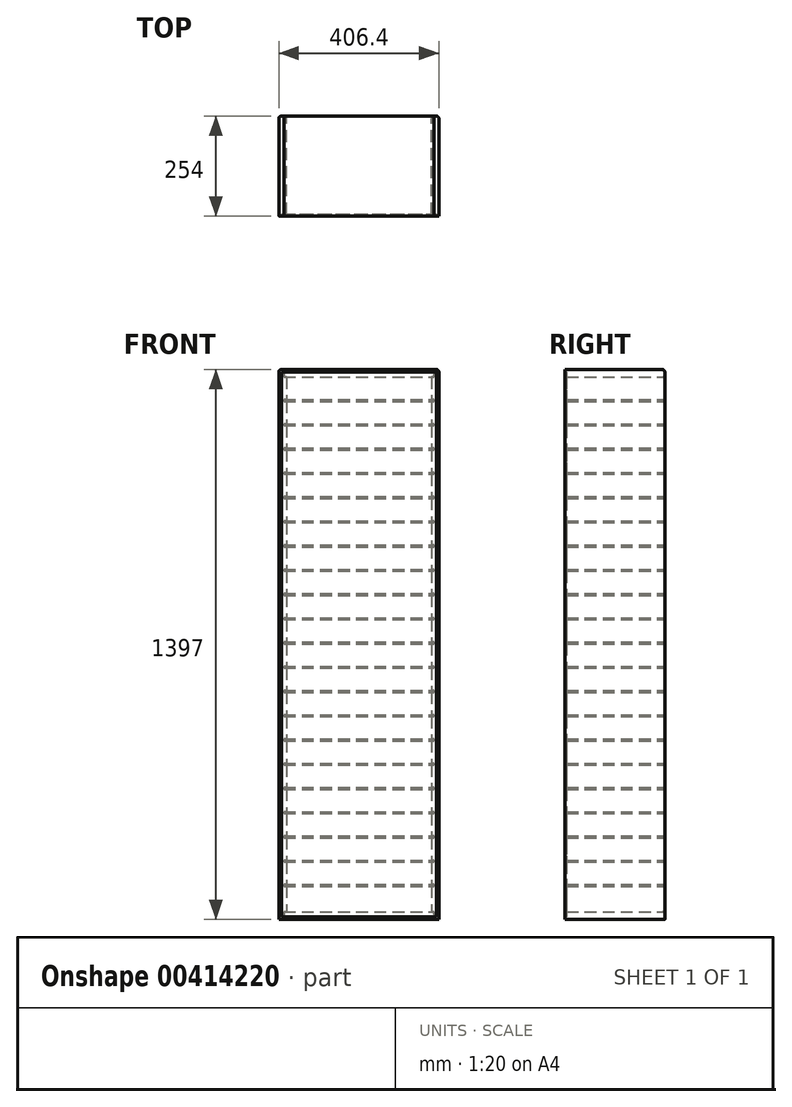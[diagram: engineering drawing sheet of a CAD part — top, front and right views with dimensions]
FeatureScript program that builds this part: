
annotation { "Feature Type Name" : "Feature", "Feature Type Description" : "" }
export const myFeature = defineFeature(function(context is Context, id is Id, definition is map)
    precondition{}
    {
        {
            var Q0;
            Q0=qCreatedBy(makeId("Front.planeOp"),FACE);
            var sketch = newSketch(context, id + "F0", { "sketchPlane" : qUnion([Q0])});
            skLineSegment(sketch, "E0.left", {"start": v(831.85, 679.45) * mm, "end": v(831.85, -679.45) * mm});
            skLineSegment(sketch, "E0.right", {"start": v(1200.15, 679.45) * mm, "end": v(1200.15, -679.45) * mm});
            skLineSegment(sketch, "E1.bottom", {"start": v(812.8, 698.5) * mm, "end": v(1219.2, 698.5) * mm});
            skLineSegment(sketch, "E1.top", {"start": v(812.8, -698.5) * mm, "end": v(1219.2, -698.5) * mm});
            skLineSegment(sketch, "E2.0", {"start": v(825.5, 679.45) * mm, "end": v(1206.5, 679.45) * mm});
            skLineSegment(sketch, "E3.bottom", {"start": v(825.5, 622.3) * mm, "end": v(1206.5, 622.3) * mm});
            skLineSegment(sketch, "E3.top", {"start": v(825.5, 617.86) * mm, "end": v(1206.5, 617.86) * mm});
            skLineSegment(sketch, "E4", {"start": v(825.5, 698.5) * mm, "end": v(825.5, 679.45) * mm});
            skLineSegment(sketch, "E5", {"start": v(1206.5, 698.5) * mm, "end": v(1206.5, 679.45) * mm});
            skLineSegment(sketch, "E6.trimOffspring", {"start": v(1219.2, 698.5) * mm, "end": v(1219.2, -698.5) * mm});
            skLineSegment(sketch, "E7.trimOffspring", {"start": v(812.8, 698.5) * mm, "end": v(812.8, -698.5) * mm});
            skLineSegment(sketch, "E8.0.1.0", {"start": v(825.5, 560.7) * mm, "end": v(825.5, 556.26) * mm});
            skLineSegment(sketch, "E8.0.1.1", {"start": v(825.5, 560.7) * mm, "end": v(1206.5, 560.7) * mm});
            skLineSegment(sketch, "E8.0.1.2", {"start": v(825.5, 556.26) * mm, "end": v(1206.5, 556.26) * mm});
            skLineSegment(sketch, "E8.0.1.3", {"start": v(1206.5, 560.7) * mm, "end": v(1206.5, 556.26) * mm});
            skLineSegment(sketch, "E8.0.2.0", {"start": v(825.5, 499.1) * mm, "end": v(825.5, 494.66) * mm});
            skLineSegment(sketch, "E8.0.2.1", {"start": v(825.5, 499.1) * mm, "end": v(1206.5, 499.1) * mm});
            skLineSegment(sketch, "E8.0.2.2", {"start": v(825.5, 494.66) * mm, "end": v(1206.5, 494.66) * mm});
            skLineSegment(sketch, "E8.0.2.3", {"start": v(1206.5, 499.1) * mm, "end": v(1206.5, 494.66) * mm});
            skLineSegment(sketch, "E8.0.3.0", {"start": v(825.5, 437.51) * mm, "end": v(825.5, 433.07) * mm});
            skLineSegment(sketch, "E8.0.3.1", {"start": v(825.5, 437.51) * mm, "end": v(1206.5, 437.51) * mm});
            skLineSegment(sketch, "E8.0.3.2", {"start": v(825.5, 433.07) * mm, "end": v(1206.5, 433.07) * mm});
            skLineSegment(sketch, "E8.0.3.3", {"start": v(1206.5, 437.51) * mm, "end": v(1206.5, 433.07) * mm});
            skLineSegment(sketch, "E8.0.4.0", {"start": v(825.5, 375.92) * mm, "end": v(825.5, 371.48) * mm});
            skLineSegment(sketch, "E8.0.4.1", {"start": v(825.5, 375.92) * mm, "end": v(1206.5, 375.92) * mm});
            skLineSegment(sketch, "E8.0.4.2", {"start": v(825.5, 371.48) * mm, "end": v(1206.5, 371.48) * mm});
            skLineSegment(sketch, "E8.0.4.3", {"start": v(1206.5, 375.92) * mm, "end": v(1206.5, 371.48) * mm});
            skLineSegment(sketch, "E8.0.5.0", {"start": v(825.5, 314.33) * mm, "end": v(825.5, 309.88) * mm});
            skLineSegment(sketch, "E8.0.5.1", {"start": v(825.5, 314.33) * mm, "end": v(1206.5, 314.33) * mm});
            skLineSegment(sketch, "E8.0.5.2", {"start": v(825.5, 309.88) * mm, "end": v(1206.5, 309.88) * mm});
            skLineSegment(sketch, "E8.0.5.3", {"start": v(1206.5, 314.33) * mm, "end": v(1206.5, 309.88) * mm});
            skLineSegment(sketch, "E8.0.6.0", {"start": v(825.5, 252.73) * mm, "end": v(825.5, 248.29) * mm});
            skLineSegment(sketch, "E8.0.6.1", {"start": v(825.5, 252.73) * mm, "end": v(1206.5, 252.73) * mm});
            skLineSegment(sketch, "E8.0.6.2", {"start": v(825.5, 248.29) * mm, "end": v(1206.5, 248.29) * mm});
            skLineSegment(sketch, "E8.0.6.3", {"start": v(1206.5, 252.73) * mm, "end": v(1206.5, 248.29) * mm});
            skLineSegment(sketch, "E8.0.7.0", {"start": v(825.5, 191.14) * mm, "end": v(825.5, 186.7) * mm});
            skLineSegment(sketch, "E8.0.7.1", {"start": v(825.5, 191.14) * mm, "end": v(1206.5, 191.14) * mm});
            skLineSegment(sketch, "E8.0.7.2", {"start": v(825.5, 186.7) * mm, "end": v(1206.5, 186.7) * mm});
            skLineSegment(sketch, "E8.0.7.3", {"start": v(1206.5, 191.14) * mm, "end": v(1206.5, 186.7) * mm});
            skLineSegment(sketch, "E8.0.8.0", {"start": v(825.5, 129.54) * mm, "end": v(825.5, 125.1) * mm});
            skLineSegment(sketch, "E8.0.8.1", {"start": v(825.5, 129.54) * mm, "end": v(1206.5, 129.54) * mm});
            skLineSegment(sketch, "E8.0.8.2", {"start": v(825.5, 125.1) * mm, "end": v(1206.5, 125.1) * mm});
            skLineSegment(sketch, "E8.0.8.3", {"start": v(1206.5, 129.54) * mm, "end": v(1206.5, 125.1) * mm});
            skLineSegment(sketch, "E8.0.9.0", {"start": v(825.5, 67.95) * mm, "end": v(825.5, 63.5) * mm});
            skLineSegment(sketch, "E8.0.9.1", {"start": v(825.5, 67.95) * mm, "end": v(1206.5, 67.95) * mm});
            skLineSegment(sketch, "E8.0.9.2", {"start": v(825.5, 63.5) * mm, "end": v(1206.5, 63.5) * mm});
            skLineSegment(sketch, "E8.0.9.3", {"start": v(1206.5, 67.95) * mm, "end": v(1206.5, 63.5) * mm});
            skLineSegment(sketch, "E8.0.10.0", {"start": v(825.5, 6.35) * mm, "end": v(825.5, 1.9) * mm});
            skLineSegment(sketch, "E8.0.10.1", {"start": v(825.5, 6.35) * mm, "end": v(1206.5, 6.35) * mm});
            skLineSegment(sketch, "E8.0.10.2", {"start": v(825.5, 1.9) * mm, "end": v(1206.5, 1.9) * mm});
            skLineSegment(sketch, "E8.0.10.3", {"start": v(1206.5, 6.35) * mm, "end": v(1206.5, 1.9) * mm});
            skLineSegment(sketch, "E8.0.11.0", {"start": v(825.5, -55.24) * mm, "end": v(825.5, -59.69) * mm});
            skLineSegment(sketch, "E8.0.11.1", {"start": v(825.5, -55.24) * mm, "end": v(1206.5, -55.24) * mm});
            skLineSegment(sketch, "E8.0.11.2", {"start": v(825.5, -59.69) * mm, "end": v(1206.5, -59.69) * mm});
            skLineSegment(sketch, "E8.0.11.3", {"start": v(1206.5, -55.24) * mm, "end": v(1206.5, -59.69) * mm});
            skLineSegment(sketch, "E8.0.12.0", {"start": v(825.5, -116.84) * mm, "end": v(825.5, -121.28) * mm});
            skLineSegment(sketch, "E8.0.12.1", {"start": v(825.5, -116.84) * mm, "end": v(1206.5, -116.84) * mm});
            skLineSegment(sketch, "E8.0.12.2", {"start": v(825.5, -121.28) * mm, "end": v(1206.5, -121.28) * mm});
            skLineSegment(sketch, "E8.0.12.3", {"start": v(1206.5, -116.84) * mm, "end": v(1206.5, -121.28) * mm});
            skLineSegment(sketch, "E8.0.13.0", {"start": v(825.5, -178.43) * mm, "end": v(825.5, -182.88) * mm});
            skLineSegment(sketch, "E8.0.13.1", {"start": v(825.5, -178.43) * mm, "end": v(1206.5, -178.43) * mm});
            skLineSegment(sketch, "E8.0.13.2", {"start": v(825.5, -182.88) * mm, "end": v(1206.5, -182.88) * mm});
            skLineSegment(sketch, "E8.0.13.3", {"start": v(1206.5, -178.43) * mm, "end": v(1206.5, -182.88) * mm});
            skLineSegment(sketch, "E8.0.14.0", {"start": v(825.5, -240.03) * mm, "end": v(825.5, -244.47) * mm});
            skLineSegment(sketch, "E8.0.14.1", {"start": v(825.5, -240.03) * mm, "end": v(1206.5, -240.03) * mm});
            skLineSegment(sketch, "E8.0.14.2", {"start": v(825.5, -244.47) * mm, "end": v(1206.5, -244.47) * mm});
            skLineSegment(sketch, "E8.0.14.3", {"start": v(1206.5, -240.03) * mm, "end": v(1206.5, -244.47) * mm});
            skLineSegment(sketch, "E8.0.15.0", {"start": v(825.5, -301.62) * mm, "end": v(825.5, -306.07) * mm});
            skLineSegment(sketch, "E8.0.15.1", {"start": v(825.5, -301.62) * mm, "end": v(1206.5, -301.62) * mm});
            skLineSegment(sketch, "E8.0.15.2", {"start": v(825.5, -306.07) * mm, "end": v(1206.5, -306.07) * mm});
            skLineSegment(sketch, "E8.0.15.3", {"start": v(1206.5, -301.62) * mm, "end": v(1206.5, -306.07) * mm});
            skLineSegment(sketch, "E8.0.16.0", {"start": v(825.5, -363.22) * mm, "end": v(825.5, -367.66) * mm});
            skLineSegment(sketch, "E8.0.16.1", {"start": v(825.5, -363.22) * mm, "end": v(1206.5, -363.22) * mm});
            skLineSegment(sketch, "E8.0.16.2", {"start": v(825.5, -367.66) * mm, "end": v(1206.5, -367.66) * mm});
            skLineSegment(sketch, "E8.0.16.3", {"start": v(1206.5, -363.22) * mm, "end": v(1206.5, -367.66) * mm});
            skLineSegment(sketch, "E8.0.17.0", {"start": v(825.5, -424.81) * mm, "end": v(825.5, -429.26) * mm});
            skLineSegment(sketch, "E8.0.17.1", {"start": v(825.5, -424.81) * mm, "end": v(1206.5, -424.81) * mm});
            skLineSegment(sketch, "E8.0.17.2", {"start": v(825.5, -429.26) * mm, "end": v(1206.5, -429.26) * mm});
            skLineSegment(sketch, "E8.0.17.3", {"start": v(1206.5, -424.81) * mm, "end": v(1206.5, -429.26) * mm});
            skLineSegment(sketch, "E8.0.18.0", {"start": v(825.5, -486.4) * mm, "end": v(825.5, -490.85) * mm});
            skLineSegment(sketch, "E8.0.18.1", {"start": v(825.5, -486.4) * mm, "end": v(1206.5, -486.4) * mm});
            skLineSegment(sketch, "E8.0.18.2", {"start": v(825.5, -490.85) * mm, "end": v(1206.5, -490.85) * mm});
            skLineSegment(sketch, "E8.0.18.3", {"start": v(1206.5, -486.4) * mm, "end": v(1206.5, -490.85) * mm});
            skLineSegment(sketch, "E8.0.19.0", {"start": v(825.5, -548) * mm, "end": v(825.5, -552.45) * mm});
            skLineSegment(sketch, "E8.0.19.1", {"start": v(825.5, -548) * mm, "end": v(1206.5, -548) * mm});
            skLineSegment(sketch, "E8.0.19.2", {"start": v(825.5, -552.45) * mm, "end": v(1206.5, -552.45) * mm});
            skLineSegment(sketch, "E8.0.19.3", {"start": v(1206.5, -548) * mm, "end": v(1206.5, -552.45) * mm});
            skLineSegment(sketch, "E8.0.20.0", {"start": v(825.5, -609.6) * mm, "end": v(825.5, -614.04) * mm});
            skLineSegment(sketch, "E8.0.20.1", {"start": v(825.5, -609.6) * mm, "end": v(1206.5, -609.6) * mm});
            skLineSegment(sketch, "E8.0.20.2", {"start": v(825.5, -614.04) * mm, "end": v(1206.5, -614.04) * mm});
            skLineSegment(sketch, "E8.0.20.3", {"start": v(1206.5, -679.45) * mm, "end": v(1206.5, -698.5) * mm});
            skLineSegment(sketch, "E8.direction1", {"start": v(825.5, 617.86) * mm, "end": v(850.9, 617.86) * mm, "construction": true});
            skLineSegment(sketch, "E9.trimOffspring", {"start": v(825.5, -679.45) * mm, "end": v(1206.5, -679.45) * mm});
            skLineSegment(sketch, "E10.trimOffspring", {"start": v(825.5, -679.45) * mm, "end": v(825.5, -698.5) * mm});
            skLineSegment(sketch, "E11", {"start": v(1206.5, -609.6) * mm, "end": v(1206.5, -614.04) * mm});
            skLineSegment(sketch, "E12.trimOffspring", {"start": v(825.5, 622.3) * mm, "end": v(825.5, 617.86) * mm});
            skLineSegment(sketch, "E13.trimOffspring", {"start": v(1206.5, 622.3) * mm, "end": v(1206.5, 617.86) * mm});
            skLineSegment(sketch, "E14", {"start": v(1219.2, 12.7) * mm, "end": v(2036.37, 12.7) * mm});
            skSolve(sketch);
        }
        {
            var Q0;
            {var subQ39=sQuery(id+"F0.wireOp",EDGE,"E4");Q0=makeQuery(id+"F0.imprint","IMPRINT",FACE,{"disambiguationData":[TD([[makeQuery(id+"F0.imprint","IMPRINT",EDGE,{"derivedFrom":subQ39}),-1.0]])]});}
            var Q1;
            {var subQ35=sQuery(id+"F0.wireOp",EDGE,"E5");Q1=makeQuery(id+"F0.imprint","IMPRINT",FACE,{"disambiguationData":[TD([[makeQuery(id+"F0.imprint","IMPRINT",EDGE,{"derivedFrom":subQ35}),1.0]])]});}
            extrude(context, id + "F1", {"entities" : qUnion([Q0, Q1]), "depth" : 254 * mm});
        }
        {
            var Q0;
            {var subQ4=sQuery(id+"F0.wireOp",EDGE,"E8.0.20.3");Q0=makeQuery(id+"F0.imprint","IMPRINT",FACE,{"disambiguationData":[TD([[makeQuery(id+"F0.imprint","IMPRINT",EDGE,{"derivedFrom":subQ4}),-1.0]])]});}
            var Q1;
            {var subQ4=sQuery(id+"F0.wireOp",EDGE,"E4");Q1=makeQuery(id+"F0.imprint","IMPRINT",FACE,{"disambiguationData":[TD([[makeQuery(id+"F0.imprint","IMPRINT",EDGE,{"derivedFrom":subQ4}),1.0]])]});}
            extrude(context, id + "F2", {"entities" : qUnion([Q0, Q1]), "depth" : 254 * mm});
        }
        {
            var Q0;
            {var subQ0=sQuery(id+"F0.wireOp",EDGE,"E3.bottom");var subQ1=sQuery(id+"F0.wireOp",EDGE,"E0.left");var subQ2=makeQuery(id+"F0.imprint","INTERSECT",VERTEX,{"derivedFrom":[subQ1,subQ0]});Q0=makeQuery(id+"F0.imprint","IMPRINT",FACE,{"disambiguationData":[TD([[makeQuery(id+"F0.imprint","IMPRINT",EDGE,{"disambiguationData":[TD([[subQ2,-1.0]])],"derivedFrom":subQ1}),1.0]])]});}
            var Q1;
            {var subQ0=sQuery(id+"F0.wireOp",EDGE,"E8.0.1.1");var subQ1=sQuery(id+"F0.wireOp",EDGE,"E0.left");var subQ2=makeQuery(id+"F0.imprint","INTERSECT",VERTEX,{"derivedFrom":[subQ1,subQ0]});Q1=makeQuery(id+"F0.imprint","IMPRINT",FACE,{"disambiguationData":[TD([[makeQuery(id+"F0.imprint","IMPRINT",EDGE,{"disambiguationData":[TD([[subQ2,-1.0]])],"derivedFrom":subQ1}),1.0]])]});}
            var Q2;
            {var subQ0=sQuery(id+"F0.wireOp",EDGE,"E8.0.2.1");var subQ1=sQuery(id+"F0.wireOp",EDGE,"E0.left");var subQ2=makeQuery(id+"F0.imprint","INTERSECT",VERTEX,{"derivedFrom":[subQ1,subQ0]});Q2=makeQuery(id+"F0.imprint","IMPRINT",FACE,{"disambiguationData":[TD([[makeQuery(id+"F0.imprint","IMPRINT",EDGE,{"disambiguationData":[TD([[subQ2,-1.0]])],"derivedFrom":subQ1}),1.0]])]});}
            var Q3;
            {var subQ0=sQuery(id+"F0.wireOp",EDGE,"E8.0.3.1");var subQ1=sQuery(id+"F0.wireOp",EDGE,"E0.left");var subQ2=makeQuery(id+"F0.imprint","INTERSECT",VERTEX,{"derivedFrom":[subQ1,subQ0]});Q3=makeQuery(id+"F0.imprint","IMPRINT",FACE,{"disambiguationData":[TD([[makeQuery(id+"F0.imprint","IMPRINT",EDGE,{"disambiguationData":[TD([[subQ2,-1.0]])],"derivedFrom":subQ1}),1.0]])]});}
            var Q4;
            {var subQ0=sQuery(id+"F0.wireOp",EDGE,"E8.0.4.1");var subQ1=sQuery(id+"F0.wireOp",EDGE,"E0.left");var subQ2=makeQuery(id+"F0.imprint","INTERSECT",VERTEX,{"derivedFrom":[subQ1,subQ0]});Q4=makeQuery(id+"F0.imprint","IMPRINT",FACE,{"disambiguationData":[TD([[makeQuery(id+"F0.imprint","IMPRINT",EDGE,{"disambiguationData":[TD([[subQ2,-1.0]])],"derivedFrom":subQ1}),1.0]])]});}
            var Q5;
            {var subQ0=sQuery(id+"F0.wireOp",EDGE,"E8.0.5.1");var subQ1=sQuery(id+"F0.wireOp",EDGE,"E0.left");var subQ2=makeQuery(id+"F0.imprint","INTERSECT",VERTEX,{"derivedFrom":[subQ1,subQ0]});Q5=makeQuery(id+"F0.imprint","IMPRINT",FACE,{"disambiguationData":[TD([[makeQuery(id+"F0.imprint","IMPRINT",EDGE,{"disambiguationData":[TD([[subQ2,-1.0]])],"derivedFrom":subQ1}),1.0]])]});}
            var Q6;
            {var subQ5=sQuery(id+"F0.wireOp",EDGE,"E13.trimOffspring");Q6=makeQuery(id+"F0.imprint","IMPRINT",FACE,{"disambiguationData":[TD([[makeQuery(id+"F0.imprint","IMPRINT",EDGE,{"derivedFrom":subQ5}),-1.0]])]});}
            var Q7;
            {var subQ5=sQuery(id+"F0.wireOp",EDGE,"E12.trimOffspring");Q7=makeQuery(id+"F0.imprint","IMPRINT",FACE,{"disambiguationData":[TD([[makeQuery(id+"F0.imprint","IMPRINT",EDGE,{"derivedFrom":subQ5}),1.0]])]});}
            var Q8;
            {var subQ5=sQuery(id+"F0.wireOp",EDGE,"E8.0.1.0");Q8=makeQuery(id+"F0.imprint","IMPRINT",FACE,{"disambiguationData":[TD([[makeQuery(id+"F0.imprint","IMPRINT",EDGE,{"derivedFrom":subQ5}),1.0]])]});}
            var Q9;
            {var subQ5=sQuery(id+"F0.wireOp",EDGE,"E8.0.1.3");Q9=makeQuery(id+"F0.imprint","IMPRINT",FACE,{"disambiguationData":[TD([[makeQuery(id+"F0.imprint","IMPRINT",EDGE,{"derivedFrom":subQ5}),-1.0]])]});}
            var Q10;
            {var subQ5=sQuery(id+"F0.wireOp",EDGE,"E8.0.2.3");Q10=makeQuery(id+"F0.imprint","IMPRINT",FACE,{"disambiguationData":[TD([[makeQuery(id+"F0.imprint","IMPRINT",EDGE,{"derivedFrom":subQ5}),-1.0]])]});}
            var Q11;
            {var subQ5=sQuery(id+"F0.wireOp",EDGE,"E8.0.2.0");Q11=makeQuery(id+"F0.imprint","IMPRINT",FACE,{"disambiguationData":[TD([[makeQuery(id+"F0.imprint","IMPRINT",EDGE,{"derivedFrom":subQ5}),1.0]])]});}
            var Q12;
            {var subQ5=sQuery(id+"F0.wireOp",EDGE,"E8.0.3.0");Q12=makeQuery(id+"F0.imprint","IMPRINT",FACE,{"disambiguationData":[TD([[makeQuery(id+"F0.imprint","IMPRINT",EDGE,{"derivedFrom":subQ5}),1.0]])]});}
            var Q13;
            {var subQ5=sQuery(id+"F0.wireOp",EDGE,"E8.0.3.3");Q13=makeQuery(id+"F0.imprint","IMPRINT",FACE,{"disambiguationData":[TD([[makeQuery(id+"F0.imprint","IMPRINT",EDGE,{"derivedFrom":subQ5}),-1.0]])]});}
            var Q14;
            {var subQ5=sQuery(id+"F0.wireOp",EDGE,"E8.0.4.3");Q14=makeQuery(id+"F0.imprint","IMPRINT",FACE,{"disambiguationData":[TD([[makeQuery(id+"F0.imprint","IMPRINT",EDGE,{"derivedFrom":subQ5}),-1.0]])]});}
            var Q15;
            {var subQ5=sQuery(id+"F0.wireOp",EDGE,"E8.0.4.0");Q15=makeQuery(id+"F0.imprint","IMPRINT",FACE,{"disambiguationData":[TD([[makeQuery(id+"F0.imprint","IMPRINT",EDGE,{"derivedFrom":subQ5}),1.0]])]});}
            var Q16;
            {var subQ5=sQuery(id+"F0.wireOp",EDGE,"E8.0.5.3");Q16=makeQuery(id+"F0.imprint","IMPRINT",FACE,{"disambiguationData":[TD([[makeQuery(id+"F0.imprint","IMPRINT",EDGE,{"derivedFrom":subQ5}),-1.0]])]});}
            var Q17;
            {var subQ5=sQuery(id+"F0.wireOp",EDGE,"E8.0.5.0");Q17=makeQuery(id+"F0.imprint","IMPRINT",FACE,{"disambiguationData":[TD([[makeQuery(id+"F0.imprint","IMPRINT",EDGE,{"derivedFrom":subQ5}),1.0]])]});}
            var Q18;
            {var subQ5=sQuery(id+"F0.wireOp",EDGE,"E8.0.6.0");Q18=makeQuery(id+"F0.imprint","IMPRINT",FACE,{"disambiguationData":[TD([[makeQuery(id+"F0.imprint","IMPRINT",EDGE,{"derivedFrom":subQ5}),1.0]])]});}
            var Q19;
            {var subQ0=sQuery(id+"F0.wireOp",EDGE,"E8.0.6.1");var subQ1=sQuery(id+"F0.wireOp",EDGE,"E0.left");var subQ2=makeQuery(id+"F0.imprint","INTERSECT",VERTEX,{"derivedFrom":[subQ1,subQ0]});Q19=makeQuery(id+"F0.imprint","IMPRINT",FACE,{"disambiguationData":[TD([[makeQuery(id+"F0.imprint","IMPRINT",EDGE,{"disambiguationData":[TD([[subQ2,-1.0]])],"derivedFrom":subQ1}),1.0]])]});}
            var Q20;
            {var subQ5=sQuery(id+"F0.wireOp",EDGE,"E8.0.6.3");Q20=makeQuery(id+"F0.imprint","IMPRINT",FACE,{"disambiguationData":[TD([[makeQuery(id+"F0.imprint","IMPRINT",EDGE,{"derivedFrom":subQ5}),-1.0]])]});}
            var Q21;
            {var subQ5=sQuery(id+"F0.wireOp",EDGE,"E8.0.7.3");Q21=makeQuery(id+"F0.imprint","IMPRINT",FACE,{"disambiguationData":[TD([[makeQuery(id+"F0.imprint","IMPRINT",EDGE,{"derivedFrom":subQ5}),-1.0]])]});}
            var Q22;
            {var subQ0=sQuery(id+"F0.wireOp",EDGE,"E8.0.7.1");var subQ1=sQuery(id+"F0.wireOp",EDGE,"E0.left");var subQ2=makeQuery(id+"F0.imprint","INTERSECT",VERTEX,{"derivedFrom":[subQ1,subQ0]});Q22=makeQuery(id+"F0.imprint","IMPRINT",FACE,{"disambiguationData":[TD([[makeQuery(id+"F0.imprint","IMPRINT",EDGE,{"disambiguationData":[TD([[subQ2,-1.0]])],"derivedFrom":subQ1}),1.0]])]});}
            var Q23;
            {var subQ5=sQuery(id+"F0.wireOp",EDGE,"E8.0.7.0");Q23=makeQuery(id+"F0.imprint","IMPRINT",FACE,{"disambiguationData":[TD([[makeQuery(id+"F0.imprint","IMPRINT",EDGE,{"derivedFrom":subQ5}),1.0]])]});}
            var Q24;
            {var subQ5=sQuery(id+"F0.wireOp",EDGE,"E8.0.8.3");Q24=makeQuery(id+"F0.imprint","IMPRINT",FACE,{"disambiguationData":[TD([[makeQuery(id+"F0.imprint","IMPRINT",EDGE,{"derivedFrom":subQ5}),-1.0]])]});}
            var Q25;
            {var subQ0=sQuery(id+"F0.wireOp",EDGE,"E8.0.8.1");var subQ1=sQuery(id+"F0.wireOp",EDGE,"E0.left");var subQ2=makeQuery(id+"F0.imprint","INTERSECT",VERTEX,{"derivedFrom":[subQ1,subQ0]});Q25=makeQuery(id+"F0.imprint","IMPRINT",FACE,{"disambiguationData":[TD([[makeQuery(id+"F0.imprint","IMPRINT",EDGE,{"disambiguationData":[TD([[subQ2,-1.0]])],"derivedFrom":subQ1}),1.0]])]});}
            var Q26;
            {var subQ5=sQuery(id+"F0.wireOp",EDGE,"E8.0.8.0");Q26=makeQuery(id+"F0.imprint","IMPRINT",FACE,{"disambiguationData":[TD([[makeQuery(id+"F0.imprint","IMPRINT",EDGE,{"derivedFrom":subQ5}),1.0]])]});}
            var Q27;
            {var subQ5=sQuery(id+"F0.wireOp",EDGE,"E8.0.9.0");Q27=makeQuery(id+"F0.imprint","IMPRINT",FACE,{"disambiguationData":[TD([[makeQuery(id+"F0.imprint","IMPRINT",EDGE,{"derivedFrom":subQ5}),1.0]])]});}
            var Q28;
            {var subQ0=sQuery(id+"F0.wireOp",EDGE,"E8.0.9.1");var subQ1=sQuery(id+"F0.wireOp",EDGE,"E0.left");var subQ2=makeQuery(id+"F0.imprint","INTERSECT",VERTEX,{"derivedFrom":[subQ1,subQ0]});Q28=makeQuery(id+"F0.imprint","IMPRINT",FACE,{"disambiguationData":[TD([[makeQuery(id+"F0.imprint","IMPRINT",EDGE,{"disambiguationData":[TD([[subQ2,-1.0]])],"derivedFrom":subQ1}),1.0]])]});}
            var Q29;
            {var subQ5=sQuery(id+"F0.wireOp",EDGE,"E8.0.9.3");Q29=makeQuery(id+"F0.imprint","IMPRINT",FACE,{"disambiguationData":[TD([[makeQuery(id+"F0.imprint","IMPRINT",EDGE,{"derivedFrom":subQ5}),-1.0]])]});}
            var Q30;
            {var subQ5=sQuery(id+"F0.wireOp",EDGE,"E8.0.10.3");Q30=makeQuery(id+"F0.imprint","IMPRINT",FACE,{"disambiguationData":[TD([[makeQuery(id+"F0.imprint","IMPRINT",EDGE,{"derivedFrom":subQ5}),-1.0]])]});}
            var Q31;
            {var subQ0=sQuery(id+"F0.wireOp",EDGE,"E8.0.10.1");var subQ1=sQuery(id+"F0.wireOp",EDGE,"E0.left");var subQ2=makeQuery(id+"F0.imprint","INTERSECT",VERTEX,{"derivedFrom":[subQ1,subQ0]});Q31=makeQuery(id+"F0.imprint","IMPRINT",FACE,{"disambiguationData":[TD([[makeQuery(id+"F0.imprint","IMPRINT",EDGE,{"disambiguationData":[TD([[subQ2,-1.0]])],"derivedFrom":subQ1}),1.0]])]});}
            var Q32;
            {var subQ5=sQuery(id+"F0.wireOp",EDGE,"E8.0.10.0");Q32=makeQuery(id+"F0.imprint","IMPRINT",FACE,{"disambiguationData":[TD([[makeQuery(id+"F0.imprint","IMPRINT",EDGE,{"derivedFrom":subQ5}),1.0]])]});}
            var Q33;
            {var subQ5=sQuery(id+"F0.wireOp",EDGE,"E8.0.11.3");Q33=makeQuery(id+"F0.imprint","IMPRINT",FACE,{"disambiguationData":[TD([[makeQuery(id+"F0.imprint","IMPRINT",EDGE,{"derivedFrom":subQ5}),-1.0]])]});}
            var Q34;
            {var subQ0=sQuery(id+"F0.wireOp",EDGE,"E8.0.11.1");var subQ1=sQuery(id+"F0.wireOp",EDGE,"E0.left");var subQ2=makeQuery(id+"F0.imprint","INTERSECT",VERTEX,{"derivedFrom":[subQ1,subQ0]});Q34=makeQuery(id+"F0.imprint","IMPRINT",FACE,{"disambiguationData":[TD([[makeQuery(id+"F0.imprint","IMPRINT",EDGE,{"disambiguationData":[TD([[subQ2,-1.0]])],"derivedFrom":subQ1}),1.0]])]});}
            var Q35;
            {var subQ5=sQuery(id+"F0.wireOp",EDGE,"E8.0.11.0");Q35=makeQuery(id+"F0.imprint","IMPRINT",FACE,{"disambiguationData":[TD([[makeQuery(id+"F0.imprint","IMPRINT",EDGE,{"derivedFrom":subQ5}),1.0]])]});}
            var Q36;
            {var subQ5=sQuery(id+"F0.wireOp",EDGE,"E8.0.12.0");Q36=makeQuery(id+"F0.imprint","IMPRINT",FACE,{"disambiguationData":[TD([[makeQuery(id+"F0.imprint","IMPRINT",EDGE,{"derivedFrom":subQ5}),1.0]])]});}
            var Q37;
            {var subQ0=sQuery(id+"F0.wireOp",EDGE,"E8.0.12.1");var subQ1=sQuery(id+"F0.wireOp",EDGE,"E0.left");var subQ2=makeQuery(id+"F0.imprint","INTERSECT",VERTEX,{"derivedFrom":[subQ1,subQ0]});Q37=makeQuery(id+"F0.imprint","IMPRINT",FACE,{"disambiguationData":[TD([[makeQuery(id+"F0.imprint","IMPRINT",EDGE,{"disambiguationData":[TD([[subQ2,-1.0]])],"derivedFrom":subQ1}),1.0]])]});}
            var Q38;
            {var subQ5=sQuery(id+"F0.wireOp",EDGE,"E8.0.12.3");Q38=makeQuery(id+"F0.imprint","IMPRINT",FACE,{"disambiguationData":[TD([[makeQuery(id+"F0.imprint","IMPRINT",EDGE,{"derivedFrom":subQ5}),-1.0]])]});}
            var Q39;
            {var subQ5=sQuery(id+"F0.wireOp",EDGE,"E8.0.13.3");Q39=makeQuery(id+"F0.imprint","IMPRINT",FACE,{"disambiguationData":[TD([[makeQuery(id+"F0.imprint","IMPRINT",EDGE,{"derivedFrom":subQ5}),-1.0]])]});}
            var Q40;
            {var subQ0=sQuery(id+"F0.wireOp",EDGE,"E8.0.13.1");var subQ1=sQuery(id+"F0.wireOp",EDGE,"E0.left");var subQ2=makeQuery(id+"F0.imprint","INTERSECT",VERTEX,{"derivedFrom":[subQ1,subQ0]});Q40=makeQuery(id+"F0.imprint","IMPRINT",FACE,{"disambiguationData":[TD([[makeQuery(id+"F0.imprint","IMPRINT",EDGE,{"disambiguationData":[TD([[subQ2,-1.0]])],"derivedFrom":subQ1}),1.0]])]});}
            var Q41;
            {var subQ5=sQuery(id+"F0.wireOp",EDGE,"E8.0.13.0");Q41=makeQuery(id+"F0.imprint","IMPRINT",FACE,{"disambiguationData":[TD([[makeQuery(id+"F0.imprint","IMPRINT",EDGE,{"derivedFrom":subQ5}),1.0]])]});}
            var Q42;
            {var subQ5=sQuery(id+"F0.wireOp",EDGE,"E8.0.14.0");Q42=makeQuery(id+"F0.imprint","IMPRINT",FACE,{"disambiguationData":[TD([[makeQuery(id+"F0.imprint","IMPRINT",EDGE,{"derivedFrom":subQ5}),1.0]])]});}
            var Q43;
            {var subQ0=sQuery(id+"F0.wireOp",EDGE,"E8.0.14.1");var subQ1=sQuery(id+"F0.wireOp",EDGE,"E0.left");var subQ2=makeQuery(id+"F0.imprint","INTERSECT",VERTEX,{"derivedFrom":[subQ1,subQ0]});Q43=makeQuery(id+"F0.imprint","IMPRINT",FACE,{"disambiguationData":[TD([[makeQuery(id+"F0.imprint","IMPRINT",EDGE,{"disambiguationData":[TD([[subQ2,-1.0]])],"derivedFrom":subQ1}),1.0]])]});}
            var Q44;
            {var subQ5=sQuery(id+"F0.wireOp",EDGE,"E8.0.14.3");Q44=makeQuery(id+"F0.imprint","IMPRINT",FACE,{"disambiguationData":[TD([[makeQuery(id+"F0.imprint","IMPRINT",EDGE,{"derivedFrom":subQ5}),-1.0]])]});}
            var Q45;
            {var subQ5=sQuery(id+"F0.wireOp",EDGE,"E8.0.15.3");Q45=makeQuery(id+"F0.imprint","IMPRINT",FACE,{"disambiguationData":[TD([[makeQuery(id+"F0.imprint","IMPRINT",EDGE,{"derivedFrom":subQ5}),-1.0]])]});}
            var Q46;
            {var subQ0=sQuery(id+"F0.wireOp",EDGE,"E8.0.15.1");var subQ1=sQuery(id+"F0.wireOp",EDGE,"E0.left");var subQ2=makeQuery(id+"F0.imprint","INTERSECT",VERTEX,{"derivedFrom":[subQ1,subQ0]});Q46=makeQuery(id+"F0.imprint","IMPRINT",FACE,{"disambiguationData":[TD([[makeQuery(id+"F0.imprint","IMPRINT",EDGE,{"disambiguationData":[TD([[subQ2,-1.0]])],"derivedFrom":subQ1}),1.0]])]});}
            var Q47;
            {var subQ5=sQuery(id+"F0.wireOp",EDGE,"E8.0.15.0");Q47=makeQuery(id+"F0.imprint","IMPRINT",FACE,{"disambiguationData":[TD([[makeQuery(id+"F0.imprint","IMPRINT",EDGE,{"derivedFrom":subQ5}),1.0]])]});}
            var Q48;
            {var subQ0=sQuery(id+"F0.wireOp",EDGE,"E8.0.16.1");var subQ1=sQuery(id+"F0.wireOp",EDGE,"E0.left");var subQ2=makeQuery(id+"F0.imprint","INTERSECT",VERTEX,{"derivedFrom":[subQ1,subQ0]});Q48=makeQuery(id+"F0.imprint","IMPRINT",FACE,{"disambiguationData":[TD([[makeQuery(id+"F0.imprint","IMPRINT",EDGE,{"disambiguationData":[TD([[subQ2,-1.0]])],"derivedFrom":subQ1}),1.0]])]});}
            var Q49;
            {var subQ5=sQuery(id+"F0.wireOp",EDGE,"E8.0.16.3");Q49=makeQuery(id+"F0.imprint","IMPRINT",FACE,{"disambiguationData":[TD([[makeQuery(id+"F0.imprint","IMPRINT",EDGE,{"derivedFrom":subQ5}),-1.0]])]});}
            var Q50;
            {var subQ5=sQuery(id+"F0.wireOp",EDGE,"E8.0.17.3");Q50=makeQuery(id+"F0.imprint","IMPRINT",FACE,{"disambiguationData":[TD([[makeQuery(id+"F0.imprint","IMPRINT",EDGE,{"derivedFrom":subQ5}),-1.0]])]});}
            var Q51;
            {var subQ0=sQuery(id+"F0.wireOp",EDGE,"E8.0.17.1");var subQ1=sQuery(id+"F0.wireOp",EDGE,"E0.left");var subQ2=makeQuery(id+"F0.imprint","INTERSECT",VERTEX,{"derivedFrom":[subQ1,subQ0]});Q51=makeQuery(id+"F0.imprint","IMPRINT",FACE,{"disambiguationData":[TD([[makeQuery(id+"F0.imprint","IMPRINT",EDGE,{"disambiguationData":[TD([[subQ2,-1.0]])],"derivedFrom":subQ1}),1.0]])]});}
            var Q52;
            {var subQ5=sQuery(id+"F0.wireOp",EDGE,"E8.0.18.3");Q52=makeQuery(id+"F0.imprint","IMPRINT",FACE,{"disambiguationData":[TD([[makeQuery(id+"F0.imprint","IMPRINT",EDGE,{"derivedFrom":subQ5}),-1.0]])]});}
            var Q53;
            {var subQ0=sQuery(id+"F0.wireOp",EDGE,"E8.0.18.1");var subQ1=sQuery(id+"F0.wireOp",EDGE,"E0.left");var subQ2=makeQuery(id+"F0.imprint","INTERSECT",VERTEX,{"derivedFrom":[subQ1,subQ0]});Q53=makeQuery(id+"F0.imprint","IMPRINT",FACE,{"disambiguationData":[TD([[makeQuery(id+"F0.imprint","IMPRINT",EDGE,{"disambiguationData":[TD([[subQ2,-1.0]])],"derivedFrom":subQ1}),1.0]])]});}
            var Q54;
            {var subQ5=sQuery(id+"F0.wireOp",EDGE,"E8.0.16.0");Q54=makeQuery(id+"F0.imprint","IMPRINT",FACE,{"disambiguationData":[TD([[makeQuery(id+"F0.imprint","IMPRINT",EDGE,{"derivedFrom":subQ5}),1.0]])]});}
            var Q55;
            {var subQ5=sQuery(id+"F0.wireOp",EDGE,"E8.0.17.0");Q55=makeQuery(id+"F0.imprint","IMPRINT",FACE,{"disambiguationData":[TD([[makeQuery(id+"F0.imprint","IMPRINT",EDGE,{"derivedFrom":subQ5}),1.0]])]});}
            var Q56;
            {var subQ5=sQuery(id+"F0.wireOp",EDGE,"E8.0.18.0");Q56=makeQuery(id+"F0.imprint","IMPRINT",FACE,{"disambiguationData":[TD([[makeQuery(id+"F0.imprint","IMPRINT",EDGE,{"derivedFrom":subQ5}),1.0]])]});}
            var Q57;
            {var subQ5=sQuery(id+"F0.wireOp",EDGE,"E8.0.19.3");Q57=makeQuery(id+"F0.imprint","IMPRINT",FACE,{"disambiguationData":[TD([[makeQuery(id+"F0.imprint","IMPRINT",EDGE,{"derivedFrom":subQ5}),-1.0]])]});}
            var Q58;
            {var subQ0=sQuery(id+"F0.wireOp",EDGE,"E8.0.19.1");var subQ1=sQuery(id+"F0.wireOp",EDGE,"E0.left");var subQ2=makeQuery(id+"F0.imprint","INTERSECT",VERTEX,{"derivedFrom":[subQ1,subQ0]});Q58=makeQuery(id+"F0.imprint","IMPRINT",FACE,{"disambiguationData":[TD([[makeQuery(id+"F0.imprint","IMPRINT",EDGE,{"disambiguationData":[TD([[subQ2,-1.0]])],"derivedFrom":subQ1}),1.0]])]});}
            var Q59;
            {var subQ5=sQuery(id+"F0.wireOp",EDGE,"E8.0.19.0");Q59=makeQuery(id+"F0.imprint","IMPRINT",FACE,{"disambiguationData":[TD([[makeQuery(id+"F0.imprint","IMPRINT",EDGE,{"derivedFrom":subQ5}),1.0]])]});}
            var Q60;
            {var subQ0=sQuery(id+"F0.wireOp",EDGE,"E8.0.20.1");var subQ1=sQuery(id+"F0.wireOp",EDGE,"E0.left");var subQ2=makeQuery(id+"F0.imprint","INTERSECT",VERTEX,{"derivedFrom":[subQ1,subQ0]});Q60=makeQuery(id+"F0.imprint","IMPRINT",FACE,{"disambiguationData":[TD([[makeQuery(id+"F0.imprint","IMPRINT",EDGE,{"disambiguationData":[TD([[subQ2,-1.0]])],"derivedFrom":subQ1}),1.0]])]});}
            var Q61;
            {var subQ5=sQuery(id+"F0.wireOp",EDGE,"E8.0.20.0");Q61=makeQuery(id+"F0.imprint","IMPRINT",FACE,{"disambiguationData":[TD([[makeQuery(id+"F0.imprint","IMPRINT",EDGE,{"derivedFrom":subQ5}),1.0]])]});}
            var Q62;
            {var subQ5=sQuery(id+"F0.wireOp",EDGE,"E11");Q62=makeQuery(id+"F0.imprint","IMPRINT",FACE,{"disambiguationData":[TD([[makeQuery(id+"F0.imprint","IMPRINT",EDGE,{"derivedFrom":subQ5}),-1.0]])]});}
            extrude(context, id + "F3", {"entities" : qUnion([Q0, Q1, Q2, Q3, Q4, Q5, Q6, Q7, Q8, Q9, Q10, Q11, Q12, Q13, Q14, Q15, Q16, Q17, Q18, Q19, Q20, Q21, Q22, Q23, Q24, Q25, Q26, Q27, Q28, Q29, Q30, Q31, Q32, Q33, Q34, Q35, Q36, Q37, Q38, Q39, Q40, Q41, Q42, Q43, Q44, Q45, Q46, Q47, Q48, Q49, Q50, Q51, Q52, Q53, Q54, Q55, Q56, Q57, Q58, Q59, Q60, Q61, Q62]), "depth" : 254 * mm});
        }
        {
            var Q0;
            Q0=makeQuery(id+"F2.opExtrude","CAP_FACE",FACE,{"disambiguationData":[OSD([sQuery(id+"F0.wireOp",EDGE,"E1.bottom"),sQuery(id+"F0.wireOp",EDGE,"E2.0"),sQuery(id+"F0.wireOp",EDGE,"E4"),sQuery(id+"F0.wireOp",EDGE,"E5")])],"isStart":false});
            var sketch = newSketch(context, id + "F4", { "sketchPlane" : qUnion([Q0])});
            skLineSegment(sketch, "E15.0", {"start": v(812.8, 698.5) * mm, "end": v(1219.2, 698.5) * mm});
            skLineSegment(sketch, "E15.1", {"start": v(1219.2, 698.5) * mm, "end": v(1219.2, -698.5) * mm});
            skLineSegment(sketch, "E15.2", {"start": v(812.8, 698.5) * mm, "end": v(812.8, -698.5) * mm});
            skLineSegment(sketch, "E15.3", {"start": v(812.8, -698.5) * mm, "end": v(1219.2, -698.5) * mm});
            skLineSegment(sketch, "E16.0", {"start": v(819.15, 692.15) * mm, "end": v(819.15, -692.15) * mm});
            skLineSegment(sketch, "E16.1", {"start": v(819.15, 692.15) * mm, "end": v(1212.85, 692.15) * mm});
            skLineSegment(sketch, "E16.2", {"start": v(1212.85, 692.15) * mm, "end": v(1212.85, -692.15) * mm});
            skLineSegment(sketch, "E16.3", {"start": v(819.15, -692.15) * mm, "end": v(1212.85, -692.15) * mm});
            skSolve(sketch);
        }
        {
            var Q0;
            {var subQ4=sQuery(id+"F4.wireOp",EDGE,"E16.0");Q0=makeQuery(id+"F4.imprint","IMPRINT",FACE,{"disambiguationData":[TD([[makeQuery(id+"F4.imprint","IMPRINT",EDGE,{"derivedFrom":subQ4}),1.0]])]});}
            var Q1;
            {var subQ5=makeQuery(id+"F2.opExtrude","CAP_EDGE",EDGE,{"disambiguationData":[OSD([sQuery(id+"F0.wireOp",EDGE,"E2.0")])],"isStart":false});Q1=makeQuery(id+"F4.imprint","IMPRINT",FACE,{"disambiguationData":[TD([[makeQuery(id+"F4.imprint","IMPRINT",EDGE,{"derivedFrom":subQ5}),1.0]])]});}
            extrude(context, id + "F5", {"entities" : qUnion([Q0, Q1]), "oppositeDirection" : true, "depth" : 4.44 * mm});
        }
        {
            var Q0;
            Q0=makeQuery(id+"F5.opExtrude","SWEPT_BODY",BODY,{"disambiguationData":[OSD([sQuery(id+"F4.wireOp",EDGE,"E16.0"),sQuery(id+"F4.wireOp",EDGE,"E16.1"),sQuery(id+"F4.wireOp",EDGE,"E16.2"),sQuery(id+"F4.wireOp",EDGE,"E16.3")])]});
            var Q1;
            Q1=makeQuery(id+"F1.opExtrude","SWEPT_BODY",BODY,{"disambiguationData":[OSD([sQuery(id+"F0.wireOp",EDGE,"E0.left"),sQuery(id+"F0.wireOp",EDGE,"E1.bottom"),sQuery(id+"F0.wireOp",EDGE,"E1.top"),sQuery(id+"F0.wireOp",EDGE,"E2.0"),sQuery(id+"F0.wireOp",EDGE,"E3.bottom"),sQuery(id+"F0.wireOp",EDGE,"E3.top"),sQuery(id+"F0.wireOp",EDGE,"E4"),sQuery(id+"F0.wireOp",EDGE,"E7.trimOffspring"),sQuery(id+"F0.wireOp",EDGE,"E8.0.1.0"),sQuery(id+"F0.wireOp",EDGE,"E8.0.1.1"),sQuery(id+"F0.wireOp",EDGE,"E8.0.1.2"),sQuery(id+"F0.wireOp",EDGE,"E8.0.2.0"),sQuery(id+"F0.wireOp",EDGE,"E8.0.2.1"),sQuery(id+"F0.wireOp",EDGE,"E8.0.2.2"),sQuery(id+"F0.wireOp",EDGE,"E8.0.3.0"),sQuery(id+"F0.wireOp",EDGE,"E8.0.3.1"),sQuery(id+"F0.wireOp",EDGE,"E8.0.3.2"),sQuery(id+"F0.wireOp",EDGE,"E8.0.4.0"),sQuery(id+"F0.wireOp",EDGE,"E8.0.4.1"),sQuery(id+"F0.wireOp",EDGE,"E8.0.4.2"),sQuery(id+"F0.wireOp",EDGE,"E8.0.5.0"),sQuery(id+"F0.wireOp",EDGE,"E8.0.5.1"),sQuery(id+"F0.wireOp",EDGE,"E8.0.5.2"),sQuery(id+"F0.wireOp",EDGE,"E8.0.6.0"),sQuery(id+"F0.wireOp",EDGE,"E8.0.6.1"),sQuery(id+"F0.wireOp",EDGE,"E8.0.6.2"),sQuery(id+"F0.wireOp",EDGE,"E8.0.7.0"),sQuery(id+"F0.wireOp",EDGE,"E8.0.7.1"),sQuery(id+"F0.wireOp",EDGE,"E8.0.7.2"),sQuery(id+"F0.wireOp",EDGE,"E8.0.8.0"),sQuery(id+"F0.wireOp",EDGE,"E8.0.8.1"),sQuery(id+"F0.wireOp",EDGE,"E8.0.8.2"),sQuery(id+"F0.wireOp",EDGE,"E8.0.9.0"),sQuery(id+"F0.wireOp",EDGE,"E8.0.9.1"),sQuery(id+"F0.wireOp",EDGE,"E8.0.9.2"),sQuery(id+"F0.wireOp",EDGE,"E8.0.10.0"),sQuery(id+"F0.wireOp",EDGE,"E8.0.10.1"),sQuery(id+"F0.wireOp",EDGE,"E8.0.10.2"),sQuery(id+"F0.wireOp",EDGE,"E8.0.11.0"),sQuery(id+"F0.wireOp",EDGE,"E8.0.11.1"),sQuery(id+"F0.wireOp",EDGE,"E8.0.11.2"),sQuery(id+"F0.wireOp",EDGE,"E8.0.12.0"),sQuery(id+"F0.wireOp",EDGE,"E8.0.12.1"),sQuery(id+"F0.wireOp",EDGE,"E8.0.12.2"),sQuery(id+"F0.wireOp",EDGE,"E8.0.13.0"),sQuery(id+"F0.wireOp",EDGE,"E8.0.13.1"),sQuery(id+"F0.wireOp",EDGE,"E8.0.13.2"),sQuery(id+"F0.wireOp",EDGE,"E8.0.14.0"),sQuery(id+"F0.wireOp",EDGE,"E8.0.14.1"),sQuery(id+"F0.wireOp",EDGE,"E8.0.14.2"),sQuery(id+"F0.wireOp",EDGE,"E8.0.15.0"),sQuery(id+"F0.wireOp",EDGE,"E8.0.15.1"),sQuery(id+"F0.wireOp",EDGE,"E8.0.15.2"),sQuery(id+"F0.wireOp",EDGE,"E8.0.16.0"),sQuery(id+"F0.wireOp",EDGE,"E8.0.16.1"),sQuery(id+"F0.wireOp",EDGE,"E8.0.16.2"),sQuery(id+"F0.wireOp",EDGE,"E8.0.17.0"),sQuery(id+"F0.wireOp",EDGE,"E8.0.17.1"),sQuery(id+"F0.wireOp",EDGE,"E8.0.17.2"),sQuery(id+"F0.wireOp",EDGE,"E8.0.18.0"),sQuery(id+"F0.wireOp",EDGE,"E8.0.18.1"),sQuery(id+"F0.wireOp",EDGE,"E8.0.18.2"),sQuery(id+"F0.wireOp",EDGE,"E8.0.19.0"),sQuery(id+"F0.wireOp",EDGE,"E8.0.19.1"),sQuery(id+"F0.wireOp",EDGE,"E8.0.19.2"),sQuery(id+"F0.wireOp",EDGE,"E8.0.20.0"),sQuery(id+"F0.wireOp",EDGE,"E8.0.20.1"),sQuery(id+"F0.wireOp",EDGE,"E8.0.20.2"),sQuery(id+"F0.wireOp",EDGE,"E9.trimOffspring"),sQuery(id+"F0.wireOp",EDGE,"E10.trimOffspring"),sQuery(id+"F0.wireOp",EDGE,"E12.trimOffspring")])]});
            var Q2;
            Q2=makeQuery(id+"F1.opExtrude","SWEPT_BODY",BODY,{"disambiguationData":[OSD([sQuery(id+"F0.wireOp",EDGE,"E0.right"),sQuery(id+"F0.wireOp",EDGE,"E1.bottom"),sQuery(id+"F0.wireOp",EDGE,"E1.top"),sQuery(id+"F0.wireOp",EDGE,"E2.0"),sQuery(id+"F0.wireOp",EDGE,"E3.bottom"),sQuery(id+"F0.wireOp",EDGE,"E3.top"),sQuery(id+"F0.wireOp",EDGE,"E5"),sQuery(id+"F0.wireOp",EDGE,"E6.trimOffspring"),sQuery(id+"F0.wireOp",EDGE,"E8.0.1.1"),sQuery(id+"F0.wireOp",EDGE,"E8.0.1.2"),sQuery(id+"F0.wireOp",EDGE,"E8.0.1.3"),sQuery(id+"F0.wireOp",EDGE,"E8.0.2.1"),sQuery(id+"F0.wireOp",EDGE,"E8.0.2.2"),sQuery(id+"F0.wireOp",EDGE,"E8.0.2.3"),sQuery(id+"F0.wireOp",EDGE,"E8.0.3.1"),sQuery(id+"F0.wireOp",EDGE,"E8.0.3.2"),sQuery(id+"F0.wireOp",EDGE,"E8.0.3.3"),sQuery(id+"F0.wireOp",EDGE,"E8.0.4.1"),sQuery(id+"F0.wireOp",EDGE,"E8.0.4.2"),sQuery(id+"F0.wireOp",EDGE,"E8.0.4.3"),sQuery(id+"F0.wireOp",EDGE,"E8.0.5.1"),sQuery(id+"F0.wireOp",EDGE,"E8.0.5.2"),sQuery(id+"F0.wireOp",EDGE,"E8.0.5.3"),sQuery(id+"F0.wireOp",EDGE,"E8.0.6.1"),sQuery(id+"F0.wireOp",EDGE,"E8.0.6.2"),sQuery(id+"F0.wireOp",EDGE,"E8.0.6.3"),sQuery(id+"F0.wireOp",EDGE,"E8.0.7.1"),sQuery(id+"F0.wireOp",EDGE,"E8.0.7.2"),sQuery(id+"F0.wireOp",EDGE,"E8.0.7.3"),sQuery(id+"F0.wireOp",EDGE,"E8.0.8.1"),sQuery(id+"F0.wireOp",EDGE,"E8.0.8.2"),sQuery(id+"F0.wireOp",EDGE,"E8.0.8.3"),sQuery(id+"F0.wireOp",EDGE,"E8.0.9.1"),sQuery(id+"F0.wireOp",EDGE,"E8.0.9.2"),sQuery(id+"F0.wireOp",EDGE,"E8.0.9.3"),sQuery(id+"F0.wireOp",EDGE,"E8.0.10.1"),sQuery(id+"F0.wireOp",EDGE,"E8.0.10.2"),sQuery(id+"F0.wireOp",EDGE,"E8.0.10.3"),sQuery(id+"F0.wireOp",EDGE,"E8.0.11.1"),sQuery(id+"F0.wireOp",EDGE,"E8.0.11.2"),sQuery(id+"F0.wireOp",EDGE,"E8.0.11.3"),sQuery(id+"F0.wireOp",EDGE,"E8.0.12.1"),sQuery(id+"F0.wireOp",EDGE,"E8.0.12.2"),sQuery(id+"F0.wireOp",EDGE,"E8.0.12.3"),sQuery(id+"F0.wireOp",EDGE,"E8.0.13.1"),sQuery(id+"F0.wireOp",EDGE,"E8.0.13.2"),sQuery(id+"F0.wireOp",EDGE,"E8.0.13.3"),sQuery(id+"F0.wireOp",EDGE,"E8.0.14.1"),sQuery(id+"F0.wireOp",EDGE,"E8.0.14.2"),sQuery(id+"F0.wireOp",EDGE,"E8.0.14.3"),sQuery(id+"F0.wireOp",EDGE,"E8.0.15.1"),sQuery(id+"F0.wireOp",EDGE,"E8.0.15.2"),sQuery(id+"F0.wireOp",EDGE,"E8.0.15.3"),sQuery(id+"F0.wireOp",EDGE,"E8.0.16.1"),sQuery(id+"F0.wireOp",EDGE,"E8.0.16.2"),sQuery(id+"F0.wireOp",EDGE,"E8.0.16.3"),sQuery(id+"F0.wireOp",EDGE,"E8.0.17.1"),sQuery(id+"F0.wireOp",EDGE,"E8.0.17.2"),sQuery(id+"F0.wireOp",EDGE,"E8.0.17.3"),sQuery(id+"F0.wireOp",EDGE,"E8.0.18.1"),sQuery(id+"F0.wireOp",EDGE,"E8.0.18.2"),sQuery(id+"F0.wireOp",EDGE,"E8.0.18.3"),sQuery(id+"F0.wireOp",EDGE,"E8.0.19.1"),sQuery(id+"F0.wireOp",EDGE,"E8.0.19.2"),sQuery(id+"F0.wireOp",EDGE,"E8.0.19.3"),sQuery(id+"F0.wireOp",EDGE,"E8.0.20.1"),sQuery(id+"F0.wireOp",EDGE,"E8.0.20.2"),sQuery(id+"F0.wireOp",EDGE,"E8.0.20.3"),sQuery(id+"F0.wireOp",EDGE,"E9.trimOffspring"),sQuery(id+"F0.wireOp",EDGE,"E11"),sQuery(id+"F0.wireOp",EDGE,"E13.trimOffspring")])]});
            var Q3;
            Q3=makeQuery(id+"F2.opExtrude","SWEPT_BODY",BODY,{"disambiguationData":[OSD([sQuery(id+"F0.wireOp",EDGE,"E1.bottom"),sQuery(id+"F0.wireOp",EDGE,"E2.0"),sQuery(id+"F0.wireOp",EDGE,"E4"),sQuery(id+"F0.wireOp",EDGE,"E5")])]});
            var Q4;
            Q4=makeQuery(id+"F2.opExtrude","SWEPT_BODY",BODY,{"disambiguationData":[OSD([sQuery(id+"F0.wireOp",EDGE,"E1.top"),sQuery(id+"F0.wireOp",EDGE,"E8.0.20.3"),sQuery(id+"F0.wireOp",EDGE,"E9.trimOffspring"),sQuery(id+"F0.wireOp",EDGE,"E10.trimOffspring")])]});
            var Q5;
            Q5=makeQuery(id+"F3.opExtrude","SWEPT_BODY",BODY,{"disambiguationData":[OSD([sQuery(id+"F0.wireOp",EDGE,"E0.right"),sQuery(id+"F0.wireOp",EDGE,"E8.0.20.0"),sQuery(id+"F0.wireOp",EDGE,"E8.0.20.1"),sQuery(id+"F0.wireOp",EDGE,"E8.0.20.2")])]});
            var Q6;
            Q6=makeQuery(id+"F3.opExtrude","SWEPT_BODY",BODY,{"disambiguationData":[OSD([sQuery(id+"F0.wireOp",EDGE,"E3.bottom"),sQuery(id+"F0.wireOp",EDGE,"E3.top"),sQuery(id+"F0.wireOp",EDGE,"E12.trimOffspring"),sQuery(id+"F0.wireOp",EDGE,"E13.trimOffspring")])]});
            var Q7;
            Q7=makeQuery(id+"F3.opExtrude","SWEPT_BODY",BODY,{"disambiguationData":[OSD([sQuery(id+"F0.wireOp",EDGE,"E8.0.1.0"),sQuery(id+"F0.wireOp",EDGE,"E8.0.1.1"),sQuery(id+"F0.wireOp",EDGE,"E8.0.1.2"),sQuery(id+"F0.wireOp",EDGE,"E8.0.1.3")])]});
            var Q8;
            Q8=makeQuery(id+"F3.opExtrude","SWEPT_BODY",BODY,{"disambiguationData":[OSD([sQuery(id+"F0.wireOp",EDGE,"E8.0.2.0"),sQuery(id+"F0.wireOp",EDGE,"E8.0.2.1"),sQuery(id+"F0.wireOp",EDGE,"E8.0.2.2"),sQuery(id+"F0.wireOp",EDGE,"E8.0.2.3")])]});
            var Q9;
            Q9=makeQuery(id+"F3.opExtrude","SWEPT_BODY",BODY,{"disambiguationData":[OSD([sQuery(id+"F0.wireOp",EDGE,"E8.0.3.0"),sQuery(id+"F0.wireOp",EDGE,"E8.0.3.1"),sQuery(id+"F0.wireOp",EDGE,"E8.0.3.2"),sQuery(id+"F0.wireOp",EDGE,"E8.0.3.3")])]});
            var Q10;
            Q10=makeQuery(id+"F3.opExtrude","SWEPT_BODY",BODY,{"disambiguationData":[OSD([sQuery(id+"F0.wireOp",EDGE,"E8.0.4.0"),sQuery(id+"F0.wireOp",EDGE,"E8.0.4.1"),sQuery(id+"F0.wireOp",EDGE,"E8.0.4.2"),sQuery(id+"F0.wireOp",EDGE,"E8.0.4.3")])]});
            var Q11;
            Q11=makeQuery(id+"F3.opExtrude","SWEPT_BODY",BODY,{"disambiguationData":[OSD([sQuery(id+"F0.wireOp",EDGE,"E8.0.5.0"),sQuery(id+"F0.wireOp",EDGE,"E8.0.5.1"),sQuery(id+"F0.wireOp",EDGE,"E8.0.5.2"),sQuery(id+"F0.wireOp",EDGE,"E8.0.5.3")])]});
            var Q12;
            Q12=makeQuery(id+"F3.opExtrude","SWEPT_BODY",BODY,{"disambiguationData":[OSD([sQuery(id+"F0.wireOp",EDGE,"E8.0.6.0"),sQuery(id+"F0.wireOp",EDGE,"E8.0.6.1"),sQuery(id+"F0.wireOp",EDGE,"E8.0.6.2"),sQuery(id+"F0.wireOp",EDGE,"E8.0.6.3")])]});
            var Q13;
            Q13=makeQuery(id+"F3.opExtrude","SWEPT_BODY",BODY,{"disambiguationData":[OSD([sQuery(id+"F0.wireOp",EDGE,"E8.0.7.0"),sQuery(id+"F0.wireOp",EDGE,"E8.0.7.1"),sQuery(id+"F0.wireOp",EDGE,"E8.0.7.2"),sQuery(id+"F0.wireOp",EDGE,"E8.0.7.3")])]});
            var Q14;
            Q14=makeQuery(id+"F3.opExtrude","SWEPT_BODY",BODY,{"disambiguationData":[OSD([sQuery(id+"F0.wireOp",EDGE,"E8.0.8.0"),sQuery(id+"F0.wireOp",EDGE,"E8.0.8.1"),sQuery(id+"F0.wireOp",EDGE,"E8.0.8.2"),sQuery(id+"F0.wireOp",EDGE,"E8.0.8.3")])]});
            var Q15;
            Q15=makeQuery(id+"F3.opExtrude","SWEPT_BODY",BODY,{"disambiguationData":[OSD([sQuery(id+"F0.wireOp",EDGE,"E8.0.9.0"),sQuery(id+"F0.wireOp",EDGE,"E8.0.9.1"),sQuery(id+"F0.wireOp",EDGE,"E8.0.9.2"),sQuery(id+"F0.wireOp",EDGE,"E8.0.9.3")])]});
            var Q16;
            Q16=makeQuery(id+"F3.opExtrude","SWEPT_BODY",BODY,{"disambiguationData":[OSD([sQuery(id+"F0.wireOp",EDGE,"E8.0.10.0"),sQuery(id+"F0.wireOp",EDGE,"E8.0.10.1"),sQuery(id+"F0.wireOp",EDGE,"E8.0.10.2"),sQuery(id+"F0.wireOp",EDGE,"E8.0.10.3")])]});
            var Q17;
            Q17=makeQuery(id+"F3.opExtrude","SWEPT_BODY",BODY,{"disambiguationData":[OSD([sQuery(id+"F0.wireOp",EDGE,"E8.0.11.0"),sQuery(id+"F0.wireOp",EDGE,"E8.0.11.1"),sQuery(id+"F0.wireOp",EDGE,"E8.0.11.2"),sQuery(id+"F0.wireOp",EDGE,"E8.0.11.3")])]});
            var Q18;
            Q18=makeQuery(id+"F3.opExtrude","SWEPT_BODY",BODY,{"disambiguationData":[OSD([sQuery(id+"F0.wireOp",EDGE,"E8.0.12.0"),sQuery(id+"F0.wireOp",EDGE,"E8.0.12.1"),sQuery(id+"F0.wireOp",EDGE,"E8.0.12.2"),sQuery(id+"F0.wireOp",EDGE,"E8.0.12.3")])]});
            var Q19;
            Q19=makeQuery(id+"F3.opExtrude","SWEPT_BODY",BODY,{"disambiguationData":[OSD([sQuery(id+"F0.wireOp",EDGE,"E8.0.13.0"),sQuery(id+"F0.wireOp",EDGE,"E8.0.13.1"),sQuery(id+"F0.wireOp",EDGE,"E8.0.13.2"),sQuery(id+"F0.wireOp",EDGE,"E8.0.13.3")])]});
            var Q20;
            Q20=makeQuery(id+"F3.opExtrude","SWEPT_BODY",BODY,{"disambiguationData":[OSD([sQuery(id+"F0.wireOp",EDGE,"E8.0.14.0"),sQuery(id+"F0.wireOp",EDGE,"E8.0.14.1"),sQuery(id+"F0.wireOp",EDGE,"E8.0.14.2"),sQuery(id+"F0.wireOp",EDGE,"E8.0.14.3")])]});
            var Q21;
            Q21=makeQuery(id+"F3.opExtrude","SWEPT_BODY",BODY,{"disambiguationData":[OSD([sQuery(id+"F0.wireOp",EDGE,"E8.0.15.0"),sQuery(id+"F0.wireOp",EDGE,"E8.0.15.1"),sQuery(id+"F0.wireOp",EDGE,"E8.0.15.2"),sQuery(id+"F0.wireOp",EDGE,"E8.0.15.3")])]});
            var Q22;
            Q22=makeQuery(id+"F3.opExtrude","SWEPT_BODY",BODY,{"disambiguationData":[OSD([sQuery(id+"F0.wireOp",EDGE,"E8.0.16.0"),sQuery(id+"F0.wireOp",EDGE,"E8.0.16.1"),sQuery(id+"F0.wireOp",EDGE,"E8.0.16.2"),sQuery(id+"F0.wireOp",EDGE,"E8.0.16.3")])]});
            var Q23;
            Q23=makeQuery(id+"F3.opExtrude","SWEPT_BODY",BODY,{"disambiguationData":[OSD([sQuery(id+"F0.wireOp",EDGE,"E8.0.17.0"),sQuery(id+"F0.wireOp",EDGE,"E8.0.17.1"),sQuery(id+"F0.wireOp",EDGE,"E8.0.17.2"),sQuery(id+"F0.wireOp",EDGE,"E8.0.17.3")])]});
            var Q24;
            Q24=makeQuery(id+"F3.opExtrude","SWEPT_BODY",BODY,{"disambiguationData":[OSD([sQuery(id+"F0.wireOp",EDGE,"E8.0.18.0"),sQuery(id+"F0.wireOp",EDGE,"E8.0.18.1"),sQuery(id+"F0.wireOp",EDGE,"E8.0.18.2"),sQuery(id+"F0.wireOp",EDGE,"E8.0.18.3")])]});
            var Q25;
            Q25=makeQuery(id+"F3.opExtrude","SWEPT_BODY",BODY,{"disambiguationData":[OSD([sQuery(id+"F0.wireOp",EDGE,"E8.0.19.0"),sQuery(id+"F0.wireOp",EDGE,"E8.0.19.1"),sQuery(id+"F0.wireOp",EDGE,"E8.0.19.2"),sQuery(id+"F0.wireOp",EDGE,"E8.0.19.3")])]});
            booleanBodies(context, id + "F6", {"operationType" : BooleanOperationType.SUBTRACTION, "tools" : qUnion([Q0]), "targets" : qUnion([Q1, Q2, Q3, Q4, Q5, Q6, Q7, Q8, Q9, Q10, Q11, Q12, Q13, Q14, Q15, Q16, Q17, Q18, Q19, Q20, Q21, Q22, Q23, Q24, Q25]), "keepTools" : true});
        }
        {
            var Q0;
            Q0=makeQuery(id+"F2.opExtrude","CAP_EDGE",EDGE,{"disambiguationData":[OSD([sQuery(id+"F0.wireOp",EDGE,"E1.bottom")])],"isStart":true});
            var Q1;
            Q1=makeQuery(id+"F1.opExtrude","SWEPT_EDGE",EDGE,{"disambiguationData":[OSD([sQuery(id+"F0.wireOp",EDGE,"E1.bottom"),sQuery(id+"F0.wireOp",EDGE,"E6.trimOffspring")])]});
            var Q2;
            Q2=makeQuery(id+"F1.opExtrude","SWEPT_EDGE",EDGE,{"disambiguationData":[OSD([sQuery(id+"F0.wireOp",EDGE,"E1.bottom"),sQuery(id+"F0.wireOp",EDGE,"E7.trimOffspring")])]});
            var Q3;
            {var subQ0=sQuery(id+"F0.wireOp",EDGE,"E1.bottom");Q3=makeQuery(id+"F1.opExtrude","CAP_EDGE",EDGE,{"disambiguationData":[OSD([subQ0]),TDD([makeQuery(id+"F0.imprint","IMPRINT",EDGE,{"disambiguationData":[TD([[makeQuery(id+"F0.imprint","INTERSECT",VERTEX,{"derivedFrom":[subQ0,sQuery(id+"F0.wireOp",EDGE,"E7.trimOffspring")]}),-1.0]])],"derivedFrom":subQ0})])],"isStart":true});}
            var Q4;
            {var subQ0=sQuery(id+"F0.wireOp",EDGE,"E1.bottom");Q4=makeQuery(id+"F1.opExtrude","CAP_EDGE",EDGE,{"disambiguationData":[OSD([subQ0]),TDD([makeQuery(id+"F0.imprint","IMPRINT",EDGE,{"disambiguationData":[TD([[makeQuery(id+"F0.imprint","INTERSECT",VERTEX,{"derivedFrom":[subQ0,sQuery(id+"F0.wireOp",EDGE,"E6.trimOffspring")]}),1.0]])],"derivedFrom":subQ0})])],"isStart":true});}
            var Q5;
            Q5=makeQuery(id+"F1.opExtrude","CAP_EDGE",EDGE,{"disambiguationData":[OSD([sQuery(id+"F0.wireOp",EDGE,"E6.trimOffspring")])],"isStart":true});
            var Q6;
            Q6=makeQuery(id+"F1.opExtrude","CAP_EDGE",EDGE,{"disambiguationData":[OSD([sQuery(id+"F0.wireOp",EDGE,"E7.trimOffspring")])],"isStart":true});
            var Q7;
            {var subQ0=sQuery(id+"F0.wireOp",EDGE,"E0.right");Q7=makeQuery(id+"F1.opExtrude","CAP_EDGE",EDGE,{"disambiguationData":[OSD([subQ0]),TDD([makeQuery(id+"F0.imprint","IMPRINT",EDGE,{"disambiguationData":[TD([[makeQuery(id+"F0.imprint","INTERSECT",VERTEX,{"derivedFrom":[subQ0,sQuery(id+"F0.wireOp",EDGE,"E2.0")]}),-1.0]])],"derivedFrom":subQ0})])],"isStart":true});}
            var Q8;
            {var subQ0=sQuery(id+"F0.wireOp",EDGE,"E0.right");Q8=makeQuery(id+"F1.opExtrude","CAP_EDGE",EDGE,{"disambiguationData":[OSD([subQ0]),TDD([makeQuery(id+"F0.imprint","IMPRINT",EDGE,{"disambiguationData":[TD([[makeQuery(id+"F0.imprint","INTERSECT",VERTEX,{"derivedFrom":[subQ0,sQuery(id+"F0.wireOp",EDGE,"E3.top")]}),-1.0]])],"derivedFrom":subQ0})])],"isStart":true});}
            var Q9;
            {var subQ0=sQuery(id+"F0.wireOp",EDGE,"E0.left");Q9=makeQuery(id+"F1.opExtrude","CAP_EDGE",EDGE,{"disambiguationData":[OSD([subQ0]),TDD([makeQuery(id+"F0.imprint","IMPRINT",EDGE,{"disambiguationData":[TD([[makeQuery(id+"F0.imprint","INTERSECT",VERTEX,{"derivedFrom":[subQ0,sQuery(id+"F0.wireOp",EDGE,"E2.0")]}),-1.0]])],"derivedFrom":subQ0})])],"isStart":true});}
            var Q10;
            {var subQ0=sQuery(id+"F0.wireOp",EDGE,"E0.left");Q10=makeQuery(id+"F1.opExtrude","CAP_EDGE",EDGE,{"disambiguationData":[OSD([subQ0]),TDD([makeQuery(id+"F0.imprint","IMPRINT",EDGE,{"disambiguationData":[TD([[makeQuery(id+"F0.imprint","INTERSECT",VERTEX,{"derivedFrom":[subQ0,sQuery(id+"F0.wireOp",EDGE,"E3.top")]}),-1.0]])],"derivedFrom":subQ0})])],"isStart":true});}
            var Q11;
            {var subQ0=sQuery(id+"F0.wireOp",EDGE,"E0.left");Q11=makeQuery(id+"F1.opExtrude","CAP_EDGE",EDGE,{"disambiguationData":[OSD([subQ0]),TDD([makeQuery(id+"F0.imprint","IMPRINT",EDGE,{"disambiguationData":[TD([[makeQuery(id+"F0.imprint","INTERSECT",VERTEX,{"derivedFrom":[subQ0,sQuery(id+"F0.wireOp",EDGE,"E8.0.1.2")]}),-1.0]])],"derivedFrom":subQ0})])],"isStart":true});}
            var Q12;
            {var subQ0=sQuery(id+"F0.wireOp",EDGE,"E0.right");Q12=makeQuery(id+"F1.opExtrude","CAP_EDGE",EDGE,{"disambiguationData":[OSD([subQ0]),TDD([makeQuery(id+"F0.imprint","IMPRINT",EDGE,{"disambiguationData":[TD([[makeQuery(id+"F0.imprint","INTERSECT",VERTEX,{"derivedFrom":[subQ0,sQuery(id+"F0.wireOp",EDGE,"E8.0.1.2")]}),-1.0]])],"derivedFrom":subQ0})])],"isStart":true});}
            var Q13;
            {var subQ0=sQuery(id+"F0.wireOp",EDGE,"E0.right");Q13=makeQuery(id+"F1.opExtrude","CAP_EDGE",EDGE,{"disambiguationData":[OSD([subQ0]),TDD([makeQuery(id+"F0.imprint","IMPRINT",EDGE,{"disambiguationData":[TD([[makeQuery(id+"F0.imprint","INTERSECT",VERTEX,{"derivedFrom":[subQ0,sQuery(id+"F0.wireOp",EDGE,"E8.0.2.2")]}),-1.0]])],"derivedFrom":subQ0})])],"isStart":true});}
            var Q14;
            {var subQ0=sQuery(id+"F0.wireOp",EDGE,"E0.right");Q14=makeQuery(id+"F1.opExtrude","CAP_EDGE",EDGE,{"disambiguationData":[OSD([subQ0]),TDD([makeQuery(id+"F0.imprint","IMPRINT",EDGE,{"disambiguationData":[TD([[makeQuery(id+"F0.imprint","INTERSECT",VERTEX,{"derivedFrom":[subQ0,sQuery(id+"F0.wireOp",EDGE,"E8.0.3.2")]}),-1.0]])],"derivedFrom":subQ0})])],"isStart":true});}
            var Q15;
            {var subQ0=sQuery(id+"F0.wireOp",EDGE,"E0.right");Q15=makeQuery(id+"F1.opExtrude","CAP_EDGE",EDGE,{"disambiguationData":[OSD([subQ0]),TDD([makeQuery(id+"F0.imprint","IMPRINT",EDGE,{"disambiguationData":[TD([[makeQuery(id+"F0.imprint","INTERSECT",VERTEX,{"derivedFrom":[subQ0,sQuery(id+"F0.wireOp",EDGE,"E8.0.4.2")]}),-1.0]])],"derivedFrom":subQ0})])],"isStart":true});}
            var Q16;
            {var subQ0=sQuery(id+"F0.wireOp",EDGE,"E0.right");Q16=makeQuery(id+"F1.opExtrude","CAP_EDGE",EDGE,{"disambiguationData":[OSD([subQ0]),TDD([makeQuery(id+"F0.imprint","IMPRINT",EDGE,{"disambiguationData":[TD([[makeQuery(id+"F0.imprint","INTERSECT",VERTEX,{"derivedFrom":[subQ0,sQuery(id+"F0.wireOp",EDGE,"E8.0.5.2")]}),-1.0]])],"derivedFrom":subQ0})])],"isStart":true});}
            var Q17;
            {var subQ0=sQuery(id+"F0.wireOp",EDGE,"E0.right");Q17=makeQuery(id+"F1.opExtrude","CAP_EDGE",EDGE,{"disambiguationData":[OSD([subQ0]),TDD([makeQuery(id+"F0.imprint","IMPRINT",EDGE,{"disambiguationData":[TD([[makeQuery(id+"F0.imprint","INTERSECT",VERTEX,{"derivedFrom":[subQ0,sQuery(id+"F0.wireOp",EDGE,"E8.0.6.2")]}),-1.0]])],"derivedFrom":subQ0})])],"isStart":true});}
            var Q18;
            {var subQ0=sQuery(id+"F0.wireOp",EDGE,"E0.right");Q18=makeQuery(id+"F1.opExtrude","CAP_EDGE",EDGE,{"disambiguationData":[OSD([subQ0]),TDD([makeQuery(id+"F0.imprint","IMPRINT",EDGE,{"disambiguationData":[TD([[makeQuery(id+"F0.imprint","INTERSECT",VERTEX,{"derivedFrom":[subQ0,sQuery(id+"F0.wireOp",EDGE,"E8.0.7.2")]}),-1.0]])],"derivedFrom":subQ0})])],"isStart":true});}
            var Q19;
            {var subQ0=sQuery(id+"F0.wireOp",EDGE,"E0.right");Q19=makeQuery(id+"F1.opExtrude","CAP_EDGE",EDGE,{"disambiguationData":[OSD([subQ0]),TDD([makeQuery(id+"F0.imprint","IMPRINT",EDGE,{"disambiguationData":[TD([[makeQuery(id+"F0.imprint","INTERSECT",VERTEX,{"derivedFrom":[subQ0,sQuery(id+"F0.wireOp",EDGE,"E8.0.8.2")]}),-1.0]])],"derivedFrom":subQ0})])],"isStart":true});}
            var Q20;
            {var subQ0=sQuery(id+"F0.wireOp",EDGE,"E0.right");Q20=makeQuery(id+"F1.opExtrude","CAP_EDGE",EDGE,{"disambiguationData":[OSD([subQ0]),TDD([makeQuery(id+"F0.imprint","IMPRINT",EDGE,{"disambiguationData":[TD([[makeQuery(id+"F0.imprint","INTERSECT",VERTEX,{"derivedFrom":[subQ0,sQuery(id+"F0.wireOp",EDGE,"E8.0.9.2")]}),-1.0]])],"derivedFrom":subQ0})])],"isStart":true});}
            var Q21;
            {var subQ0=sQuery(id+"F0.wireOp",EDGE,"E0.right");Q21=makeQuery(id+"F1.opExtrude","CAP_EDGE",EDGE,{"disambiguationData":[OSD([subQ0]),TDD([makeQuery(id+"F0.imprint","IMPRINT",EDGE,{"disambiguationData":[TD([[makeQuery(id+"F0.imprint","INTERSECT",VERTEX,{"derivedFrom":[subQ0,sQuery(id+"F0.wireOp",EDGE,"E8.0.10.2")]}),-1.0]])],"derivedFrom":subQ0})])],"isStart":true});}
            var Q22;
            {var subQ0=sQuery(id+"F0.wireOp",EDGE,"E0.right");Q22=makeQuery(id+"F1.opExtrude","CAP_EDGE",EDGE,{"disambiguationData":[OSD([subQ0]),TDD([makeQuery(id+"F0.imprint","IMPRINT",EDGE,{"disambiguationData":[TD([[makeQuery(id+"F0.imprint","INTERSECT",VERTEX,{"derivedFrom":[subQ0,sQuery(id+"F0.wireOp",EDGE,"E8.0.11.2")]}),-1.0]])],"derivedFrom":subQ0})])],"isStart":true});}
            var Q23;
            {var subQ0=sQuery(id+"F0.wireOp",EDGE,"E0.right");Q23=makeQuery(id+"F1.opExtrude","CAP_EDGE",EDGE,{"disambiguationData":[OSD([subQ0]),TDD([makeQuery(id+"F0.imprint","IMPRINT",EDGE,{"disambiguationData":[TD([[makeQuery(id+"F0.imprint","INTERSECT",VERTEX,{"derivedFrom":[subQ0,sQuery(id+"F0.wireOp",EDGE,"E8.0.12.2")]}),-1.0]])],"derivedFrom":subQ0})])],"isStart":true});}
            var Q24;
            {var subQ0=sQuery(id+"F0.wireOp",EDGE,"E0.right");Q24=makeQuery(id+"F1.opExtrude","CAP_EDGE",EDGE,{"disambiguationData":[OSD([subQ0]),TDD([makeQuery(id+"F0.imprint","IMPRINT",EDGE,{"disambiguationData":[TD([[makeQuery(id+"F0.imprint","INTERSECT",VERTEX,{"derivedFrom":[subQ0,sQuery(id+"F0.wireOp",EDGE,"E8.0.13.2")]}),-1.0]])],"derivedFrom":subQ0})])],"isStart":true});}
            var Q25;
            {var subQ0=sQuery(id+"F0.wireOp",EDGE,"E0.right");Q25=makeQuery(id+"F1.opExtrude","CAP_EDGE",EDGE,{"disambiguationData":[OSD([subQ0]),TDD([makeQuery(id+"F0.imprint","IMPRINT",EDGE,{"disambiguationData":[TD([[makeQuery(id+"F0.imprint","INTERSECT",VERTEX,{"derivedFrom":[subQ0,sQuery(id+"F0.wireOp",EDGE,"E8.0.14.2")]}),-1.0]])],"derivedFrom":subQ0})])],"isStart":true});}
            var Q26;
            {var subQ0=sQuery(id+"F0.wireOp",EDGE,"E0.right");Q26=makeQuery(id+"F1.opExtrude","CAP_EDGE",EDGE,{"disambiguationData":[OSD([subQ0]),TDD([makeQuery(id+"F0.imprint","IMPRINT",EDGE,{"disambiguationData":[TD([[makeQuery(id+"F0.imprint","INTERSECT",VERTEX,{"derivedFrom":[subQ0,sQuery(id+"F0.wireOp",EDGE,"E8.0.15.2")]}),-1.0]])],"derivedFrom":subQ0})])],"isStart":true});}
            var Q27;
            {var subQ0=sQuery(id+"F0.wireOp",EDGE,"E0.right");Q27=makeQuery(id+"F1.opExtrude","CAP_EDGE",EDGE,{"disambiguationData":[OSD([subQ0]),TDD([makeQuery(id+"F0.imprint","IMPRINT",EDGE,{"disambiguationData":[TD([[makeQuery(id+"F0.imprint","INTERSECT",VERTEX,{"derivedFrom":[subQ0,sQuery(id+"F0.wireOp",EDGE,"E8.0.17.2")]}),-1.0]])],"derivedFrom":subQ0})])],"isStart":true});}
            var Q28;
            {var subQ0=sQuery(id+"F0.wireOp",EDGE,"E0.right");Q28=makeQuery(id+"F1.opExtrude","CAP_EDGE",EDGE,{"disambiguationData":[OSD([subQ0]),TDD([makeQuery(id+"F0.imprint","IMPRINT",EDGE,{"disambiguationData":[TD([[makeQuery(id+"F0.imprint","INTERSECT",VERTEX,{"derivedFrom":[subQ0,sQuery(id+"F0.wireOp",EDGE,"E8.0.16.2")]}),-1.0]])],"derivedFrom":subQ0})])],"isStart":true});}
            var Q29;
            {var subQ0=sQuery(id+"F0.wireOp",EDGE,"E0.right");Q29=makeQuery(id+"F1.opExtrude","CAP_EDGE",EDGE,{"disambiguationData":[OSD([subQ0]),TDD([makeQuery(id+"F0.imprint","IMPRINT",EDGE,{"disambiguationData":[TD([[makeQuery(id+"F0.imprint","INTERSECT",VERTEX,{"derivedFrom":[subQ0,sQuery(id+"F0.wireOp",EDGE,"E8.0.18.2")]}),-1.0]])],"derivedFrom":subQ0})])],"isStart":true});}
            var Q30;
            {var subQ0=sQuery(id+"F0.wireOp",EDGE,"E0.right");Q30=makeQuery(id+"F1.opExtrude","CAP_EDGE",EDGE,{"disambiguationData":[OSD([subQ0]),TDD([makeQuery(id+"F0.imprint","IMPRINT",EDGE,{"disambiguationData":[TD([[makeQuery(id+"F0.imprint","INTERSECT",VERTEX,{"derivedFrom":[subQ0,sQuery(id+"F0.wireOp",EDGE,"E8.0.19.2")]}),-1.0]])],"derivedFrom":subQ0})])],"isStart":true});}
            var Q31;
            {var subQ0=sQuery(id+"F0.wireOp",EDGE,"E0.right");Q31=makeQuery(id+"F1.opExtrude","CAP_EDGE",EDGE,{"disambiguationData":[OSD([subQ0]),TDD([makeQuery(id+"F0.imprint","IMPRINT",EDGE,{"disambiguationData":[TD([[makeQuery(id+"F0.imprint","INTERSECT",VERTEX,{"derivedFrom":[subQ0,sQuery(id+"F0.wireOp",EDGE,"E9.trimOffspring")]}),1.0]])],"derivedFrom":subQ0})])],"isStart":true});}
            var Q32;
            Q32=makeQuery(id+"F2.opExtrude","CAP_EDGE",EDGE,{"disambiguationData":[OSD([sQuery(id+"F0.wireOp",EDGE,"E9.trimOffspring")])],"isStart":true});
            var Q33;
            {var subQ0=sQuery(id+"F0.wireOp",EDGE,"E0.left");Q33=makeQuery(id+"F1.opExtrude","CAP_EDGE",EDGE,{"disambiguationData":[OSD([subQ0]),TDD([makeQuery(id+"F0.imprint","IMPRINT",EDGE,{"disambiguationData":[TD([[makeQuery(id+"F0.imprint","INTERSECT",VERTEX,{"derivedFrom":[subQ0,sQuery(id+"F0.wireOp",EDGE,"E9.trimOffspring")]}),1.0]])],"derivedFrom":subQ0})])],"isStart":true});}
            var Q34;
            {var subQ0=sQuery(id+"F0.wireOp",EDGE,"E0.left");Q34=makeQuery(id+"F1.opExtrude","CAP_EDGE",EDGE,{"disambiguationData":[OSD([subQ0]),TDD([makeQuery(id+"F0.imprint","IMPRINT",EDGE,{"disambiguationData":[TD([[makeQuery(id+"F0.imprint","INTERSECT",VERTEX,{"derivedFrom":[subQ0,sQuery(id+"F0.wireOp",EDGE,"E8.0.19.2")]}),-1.0]])],"derivedFrom":subQ0})])],"isStart":true});}
            var Q35;
            {var subQ0=sQuery(id+"F0.wireOp",EDGE,"E0.left");Q35=makeQuery(id+"F1.opExtrude","CAP_EDGE",EDGE,{"disambiguationData":[OSD([subQ0]),TDD([makeQuery(id+"F0.imprint","IMPRINT",EDGE,{"disambiguationData":[TD([[makeQuery(id+"F0.imprint","INTERSECT",VERTEX,{"derivedFrom":[subQ0,sQuery(id+"F0.wireOp",EDGE,"E8.0.18.2")]}),-1.0]])],"derivedFrom":subQ0})])],"isStart":true});}
            var Q36;
            {var subQ0=sQuery(id+"F0.wireOp",EDGE,"E0.left");Q36=makeQuery(id+"F1.opExtrude","CAP_EDGE",EDGE,{"disambiguationData":[OSD([subQ0]),TDD([makeQuery(id+"F0.imprint","IMPRINT",EDGE,{"disambiguationData":[TD([[makeQuery(id+"F0.imprint","INTERSECT",VERTEX,{"derivedFrom":[subQ0,sQuery(id+"F0.wireOp",EDGE,"E8.0.17.2")]}),-1.0]])],"derivedFrom":subQ0})])],"isStart":true});}
            var Q37;
            {var subQ0=sQuery(id+"F0.wireOp",EDGE,"E0.left");Q37=makeQuery(id+"F1.opExtrude","CAP_EDGE",EDGE,{"disambiguationData":[OSD([subQ0]),TDD([makeQuery(id+"F0.imprint","IMPRINT",EDGE,{"disambiguationData":[TD([[makeQuery(id+"F0.imprint","INTERSECT",VERTEX,{"derivedFrom":[subQ0,sQuery(id+"F0.wireOp",EDGE,"E8.0.16.2")]}),-1.0]])],"derivedFrom":subQ0})])],"isStart":true});}
            var Q38;
            {var subQ0=sQuery(id+"F0.wireOp",EDGE,"E0.left");Q38=makeQuery(id+"F1.opExtrude","CAP_EDGE",EDGE,{"disambiguationData":[OSD([subQ0]),TDD([makeQuery(id+"F0.imprint","IMPRINT",EDGE,{"disambiguationData":[TD([[makeQuery(id+"F0.imprint","INTERSECT",VERTEX,{"derivedFrom":[subQ0,sQuery(id+"F0.wireOp",EDGE,"E8.0.15.2")]}),-1.0]])],"derivedFrom":subQ0})])],"isStart":true});}
            var Q39;
            {var subQ0=sQuery(id+"F0.wireOp",EDGE,"E0.left");Q39=makeQuery(id+"F1.opExtrude","CAP_EDGE",EDGE,{"disambiguationData":[OSD([subQ0]),TDD([makeQuery(id+"F0.imprint","IMPRINT",EDGE,{"disambiguationData":[TD([[makeQuery(id+"F0.imprint","INTERSECT",VERTEX,{"derivedFrom":[subQ0,sQuery(id+"F0.wireOp",EDGE,"E8.0.14.2")]}),-1.0]])],"derivedFrom":subQ0})])],"isStart":true});}
            var Q40;
            {var subQ0=sQuery(id+"F0.wireOp",EDGE,"E0.left");Q40=makeQuery(id+"F1.opExtrude","CAP_EDGE",EDGE,{"disambiguationData":[OSD([subQ0]),TDD([makeQuery(id+"F0.imprint","IMPRINT",EDGE,{"disambiguationData":[TD([[makeQuery(id+"F0.imprint","INTERSECT",VERTEX,{"derivedFrom":[subQ0,sQuery(id+"F0.wireOp",EDGE,"E8.0.13.2")]}),-1.0]])],"derivedFrom":subQ0})])],"isStart":true});}
            var Q41;
            {var subQ0=sQuery(id+"F0.wireOp",EDGE,"E0.left");Q41=makeQuery(id+"F1.opExtrude","CAP_EDGE",EDGE,{"disambiguationData":[OSD([subQ0]),TDD([makeQuery(id+"F0.imprint","IMPRINT",EDGE,{"disambiguationData":[TD([[makeQuery(id+"F0.imprint","INTERSECT",VERTEX,{"derivedFrom":[subQ0,sQuery(id+"F0.wireOp",EDGE,"E8.0.12.2")]}),-1.0]])],"derivedFrom":subQ0})])],"isStart":true});}
            var Q42;
            {var subQ0=sQuery(id+"F0.wireOp",EDGE,"E0.left");Q42=makeQuery(id+"F1.opExtrude","CAP_EDGE",EDGE,{"disambiguationData":[OSD([subQ0]),TDD([makeQuery(id+"F0.imprint","IMPRINT",EDGE,{"disambiguationData":[TD([[makeQuery(id+"F0.imprint","INTERSECT",VERTEX,{"derivedFrom":[subQ0,sQuery(id+"F0.wireOp",EDGE,"E8.0.11.2")]}),-1.0]])],"derivedFrom":subQ0})])],"isStart":true});}
            var Q43;
            {var subQ0=sQuery(id+"F0.wireOp",EDGE,"E0.left");Q43=makeQuery(id+"F1.opExtrude","CAP_EDGE",EDGE,{"disambiguationData":[OSD([subQ0]),TDD([makeQuery(id+"F0.imprint","IMPRINT",EDGE,{"disambiguationData":[TD([[makeQuery(id+"F0.imprint","INTERSECT",VERTEX,{"derivedFrom":[subQ0,sQuery(id+"F0.wireOp",EDGE,"E8.0.10.2")]}),-1.0]])],"derivedFrom":subQ0})])],"isStart":true});}
            var Q44;
            {var subQ0=sQuery(id+"F0.wireOp",EDGE,"E0.left");Q44=makeQuery(id+"F1.opExtrude","CAP_EDGE",EDGE,{"disambiguationData":[OSD([subQ0]),TDD([makeQuery(id+"F0.imprint","IMPRINT",EDGE,{"disambiguationData":[TD([[makeQuery(id+"F0.imprint","INTERSECT",VERTEX,{"derivedFrom":[subQ0,sQuery(id+"F0.wireOp",EDGE,"E8.0.9.2")]}),-1.0]])],"derivedFrom":subQ0})])],"isStart":true});}
            var Q45;
            {var subQ0=sQuery(id+"F0.wireOp",EDGE,"E0.left");Q45=makeQuery(id+"F1.opExtrude","CAP_EDGE",EDGE,{"disambiguationData":[OSD([subQ0]),TDD([makeQuery(id+"F0.imprint","IMPRINT",EDGE,{"disambiguationData":[TD([[makeQuery(id+"F0.imprint","INTERSECT",VERTEX,{"derivedFrom":[subQ0,sQuery(id+"F0.wireOp",EDGE,"E8.0.8.2")]}),-1.0]])],"derivedFrom":subQ0})])],"isStart":true});}
            var Q46;
            {var subQ0=sQuery(id+"F0.wireOp",EDGE,"E0.left");Q46=makeQuery(id+"F1.opExtrude","CAP_EDGE",EDGE,{"disambiguationData":[OSD([subQ0]),TDD([makeQuery(id+"F0.imprint","IMPRINT",EDGE,{"disambiguationData":[TD([[makeQuery(id+"F0.imprint","INTERSECT",VERTEX,{"derivedFrom":[subQ0,sQuery(id+"F0.wireOp",EDGE,"E8.0.7.2")]}),-1.0]])],"derivedFrom":subQ0})])],"isStart":true});}
            var Q47;
            {var subQ0=sQuery(id+"F0.wireOp",EDGE,"E0.left");Q47=makeQuery(id+"F1.opExtrude","CAP_EDGE",EDGE,{"disambiguationData":[OSD([subQ0]),TDD([makeQuery(id+"F0.imprint","IMPRINT",EDGE,{"disambiguationData":[TD([[makeQuery(id+"F0.imprint","INTERSECT",VERTEX,{"derivedFrom":[subQ0,sQuery(id+"F0.wireOp",EDGE,"E8.0.6.2")]}),-1.0]])],"derivedFrom":subQ0})])],"isStart":true});}
            var Q48;
            {var subQ0=sQuery(id+"F0.wireOp",EDGE,"E0.left");Q48=makeQuery(id+"F1.opExtrude","CAP_EDGE",EDGE,{"disambiguationData":[OSD([subQ0]),TDD([makeQuery(id+"F0.imprint","IMPRINT",EDGE,{"disambiguationData":[TD([[makeQuery(id+"F0.imprint","INTERSECT",VERTEX,{"derivedFrom":[subQ0,sQuery(id+"F0.wireOp",EDGE,"E8.0.5.2")]}),-1.0]])],"derivedFrom":subQ0})])],"isStart":true});}
            var Q49;
            {var subQ0=sQuery(id+"F0.wireOp",EDGE,"E0.left");Q49=makeQuery(id+"F1.opExtrude","CAP_EDGE",EDGE,{"disambiguationData":[OSD([subQ0]),TDD([makeQuery(id+"F0.imprint","IMPRINT",EDGE,{"disambiguationData":[TD([[makeQuery(id+"F0.imprint","INTERSECT",VERTEX,{"derivedFrom":[subQ0,sQuery(id+"F0.wireOp",EDGE,"E8.0.4.2")]}),-1.0]])],"derivedFrom":subQ0})])],"isStart":true});}
            var Q50;
            {var subQ0=sQuery(id+"F0.wireOp",EDGE,"E0.left");Q50=makeQuery(id+"F1.opExtrude","CAP_EDGE",EDGE,{"disambiguationData":[OSD([subQ0]),TDD([makeQuery(id+"F0.imprint","IMPRINT",EDGE,{"disambiguationData":[TD([[makeQuery(id+"F0.imprint","INTERSECT",VERTEX,{"derivedFrom":[subQ0,sQuery(id+"F0.wireOp",EDGE,"E8.0.3.2")]}),-1.0]])],"derivedFrom":subQ0})])],"isStart":true});}
            var Q51;
            {var subQ0=sQuery(id+"F0.wireOp",EDGE,"E0.left");Q51=makeQuery(id+"F1.opExtrude","CAP_EDGE",EDGE,{"disambiguationData":[OSD([subQ0]),TDD([makeQuery(id+"F0.imprint","IMPRINT",EDGE,{"disambiguationData":[TD([[makeQuery(id+"F0.imprint","INTERSECT",VERTEX,{"derivedFrom":[subQ0,sQuery(id+"F0.wireOp",EDGE,"E8.0.2.2")]}),-1.0]])],"derivedFrom":subQ0})])],"isStart":true});}
            var Q52;
            Q52=makeQuery(id+"F2.opExtrude","CAP_EDGE",EDGE,{"disambiguationData":[OSD([sQuery(id+"F0.wireOp",EDGE,"E2.0")])],"isStart":true});
            fillet(context, id + "F7", {"entities" : qUnion([Q0, Q1, Q2, Q3, Q4, Q5, Q6, Q7, Q8, Q9, Q10, Q11, Q12, Q13, Q14, Q15, Q16, Q17, Q18, Q19, Q20, Q21, Q22, Q23, Q24, Q25, Q26, Q27, Q28, Q29, Q30, Q31, Q32, Q33, Q34, Q35, Q36, Q37, Q38, Q39, Q40, Q41, Q42, Q43, Q44, Q45, Q46, Q47, Q48, Q49, Q50, Q51, Q52]), "radius" : 6.35 * mm, "allowEdgeOverflow" : false});
        }
    });
